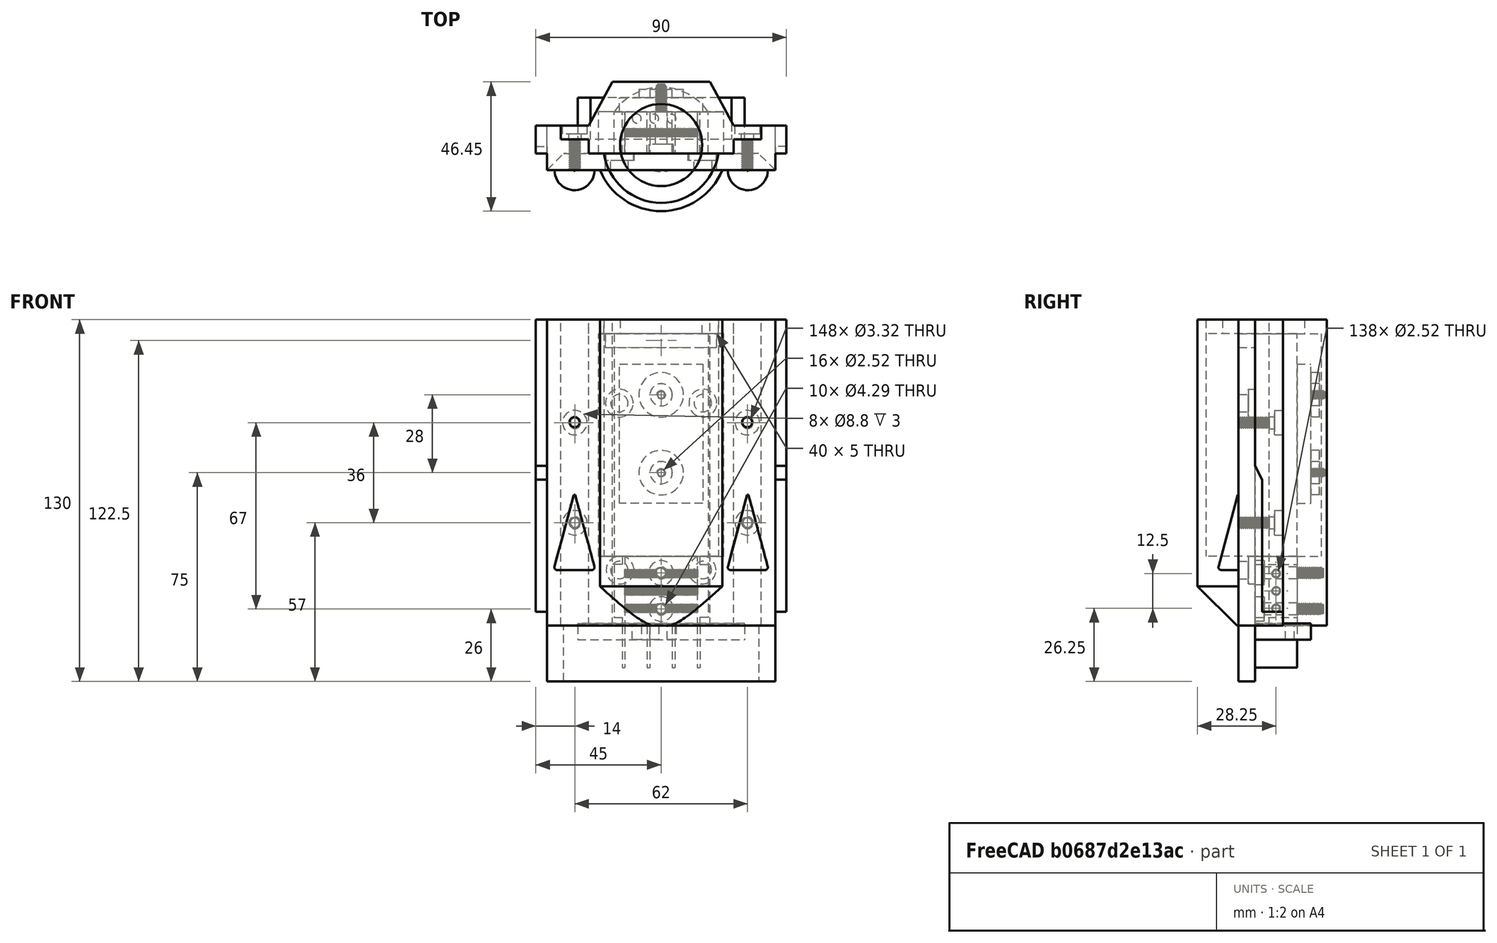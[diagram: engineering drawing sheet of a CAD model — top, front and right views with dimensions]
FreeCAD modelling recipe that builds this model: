
FCSTD DOCUMENT  (FreeCAD 2023.131R26244 +5365 (Git))
Label: Ego 56v Battery mount
License: All rights reserved
LicenseURL: http://en.wikipedia.org/wiki/All_rights_reserved
objects: Sketcher::SketchObject×39, PartDesign::Pocket×22, PartDesign::Pad×11, PartDesign::Body×7, PartDesign::Hole×6, PartDesign::Chamfer×2, Spreadsheet::Sheet×1, PartDesign::Fillet×1
note: 211 computed .brp shape members not serialized (recipe doc carries the construction recipe); baked Part::Feature solids carry a one-line shape summary decoded from their .brp

FEATURE [Sketcher::SketchObject] Sketch
  ArcFitTolerance = 1e-06
  AttachmentSupport = -> [XY_Plane]
  ExternalBSplineMaxDegree = 5
  ExternalBSplineTolerance = 0.0001
  FullyConstrained = false
  InternalTolerance = 1e-06
  InvalidShape = false
  MakeInternals = false
  MapMode = 5
  Support = -> [XY_Plane]
  TreeRank = 13
  ValidateShape = true
  sketch-geometry (12):
    g0: LineSegment StartX=-17.5 StartY=25.7 StartZ=0 EndX=17.5 EndY=25.7 EndZ=0
    g1: LineSegment StartX=-17.5 StartY=25.7 StartZ=0 EndX=-26 EndY=10 EndZ=0
    g2: LineSegment StartX=17.5 StartY=25.7 StartZ=0 EndX=26 EndY=10 EndZ=0
    g3: LineSegment StartX=-26 StartY=10 StartZ=0 EndX=-45 EndY=10 EndZ=0
    g4: LineSegment StartX=26 StartY=10 StartZ=0 EndX=45 EndY=10 EndZ=0
    g5: LineSegment StartX=-41 StartY=-6 StartZ=0 EndX=41 EndY=-6 EndZ=0
    g6: LineSegment StartX=-45 StartY=10 StartZ=0 EndX=-45 EndY=0 EndZ=0
    g7: LineSegment StartX=-45 StartY=-9e-16 StartZ=0 EndX=-41 EndY=-9e-16 EndZ=0
    g8: LineSegment StartX=-41 StartY=-6 StartZ=0 EndX=-41 EndY=-9e-16 EndZ=0
    g9: LineSegment StartX=45 StartY=10 StartZ=0 EndX=45 EndY=0 EndZ=0
    g10: LineSegment StartX=45 StartY=0 StartZ=0 EndX=41 EndY=0 EndZ=0
    g11: LineSegment StartX=41 StartY=-6 StartZ=0 EndX=41 EndY=0 EndZ=0
  constraints (33):
    c: DistanceX(g0,g0) = 35
    c: Symmetric(g0,g0,g-2)
    c: Coincident(g1,g0)
    c: Coincident(g2,g0)
    c: DistanceY(g2,g0) = 15.7
    c: Symmetric(g1,g2,g-2)
    c: DistanceX(g1,g2) = 52
    c: Coincident(g3,g1)
    c: Horizontal(g3)
    c: Coincident(g4,g2)
    c: Horizontal(g4)
    c: Equal(g3,g4)
    c: DistanceY(g5,g4) = 16
    c: DistanceX(g3,g4) = 90
    c: DistanceX(g5,g5) = 82
    c: Coincident(g6,g3)
    c: Vertical(g6)
    c: Coincident(g7,g6)
    c: Horizontal(g7)
    c: Coincident(g8,g5)
    c: Coincident(g8,g7)
    c: Vertical(g8)
    c: Coincident(g9,g4)
    c: Vertical(g9)
    c: Coincident(g10,g9)
    c: Horizontal(g10)
    c: Coincident(g11,g5)
    c: Coincident(g11,g10)
    c: Vertical(g11)
    c: Equal(g6,g9)
    c: Equal(g8,g11)
    c: DistanceY(g9,g4) = 10
    c: PointOnObject(g10,g-1)
FEATURE [PartDesign::Pad] Pad
  AddSubType = 0
  AlongSketchNormal = false
  AutoTaperInnerAngle = true
  CheckUpToFaceLimits = true
  ClaimChildren = false
  Direction = (0,0,1)
  Fit = 0
  FitJoin = 0
  InnerFit = 0
  InnerFitJoin = 0
  InvalidShape = false
  Length = 110
  Length2 = 100
  Linearize = true
  NewSolid = false
  Profile = -> Sketch
  Suppress = false
  TaperInnerAngle = 0
  TaperInnerAngleRev = 0
  TreeRank = 14
  Type = 0
  ValidateShape = true
  _ProfileBasedVersion = 1
FEATURE [Sketcher::SketchObject] Sketch001
  ArcFitTolerance = 1e-06
  AttachmentOffset = pos=(0,0,-45) rot=(0,0,1;0rad)
  AttachmentSupport = -> [YZ_Plane]
  ExternalBSplineMaxDegree = 5
  ExternalBSplineTolerance = 0.0001
  FullyConstrained = true
  InternalTolerance = 1e-06
  InvalidShape = false
  MakeInternals = false
  MapMode = 5
  Placement = pos=(-45,1e-14,-1e-14) rot=(0.57735,0.57735,0.57735;2.0944rad)
  Support = -> [YZ_Plane]
  TreeRank = 15
  ValidateShape = true
  sketch-geometry (6):
    g0: LineSegment StartX=2.5 StartY=5 StartZ=0 EndX=10 EndY=5 EndZ=0
    g1: LineSegment StartX=0 StartY=0 StartZ=0 EndX=10 EndY=0 EndZ=0
    g2: LineSegment StartX=10 StartY=5 StartZ=0 EndX=10 EndY=0 EndZ=0
    g3: LineSegment StartX=2.5 StartY=5 StartZ=0 EndX=2.5 EndY=52.5 EndZ=0
    g4: LineSegment StartX=2.5 StartY=52.5 StartZ=0 EndX=0 EndY=57.5 EndZ=0
    g5: LineSegment StartX=0 StartY=57.5 StartZ=0 EndX=0 EndY=0 EndZ=0
  constraints (17):
    c: Horizontal(g0)
    c: DistanceY(g-1,g0) = 5
    c: Coincident(g1,g-1)
    c: PointOnObject(g1,g-1)
    c: Coincident(g2,g0)
    c: Coincident(g2,g1)
    c: Vertical(g2)
    c: DistanceX(g1,g1) = 10
    c: Coincident(g3,g0)
    c: Vertical(g3)
    c: DistanceY(g1,g3) = 52.5
    c: Coincident(g4,g3)
    c: PointOnObject(g4,g-2)
    c: DistanceY(g3,g4) = 5
    c: Coincident(g5,g4)
    c: Coincident(g5,g1)
    c: DistanceX(g1,g0) = 2.5
FEATURE [PartDesign::Pocket] Pocket
  AddSubType = 1
  AutoTaperInnerAngle = true
  BaseFeature = -> Pad
  CheckUpToFaceLimits = true
  ClaimChildren = false
  Fit = 0
  FitJoin = 0
  InnerFit = 0
  InnerFitJoin = 0
  InvalidShape = false
  Length = 4
  Length2 = 100
  Linearize = true
  NewSolid = false
  Profile = -> Sketch001
  Reversed = true
  Suppress = false
  TaperInnerAngle = 0
  TaperInnerAngleRev = 0
  TreeRank = 16
  Type = 0
  ValidateShape = true
  _ProfileBasedVersion = 1
  _Version = 1
FEATURE [Sketcher::SketchObject] Sketch002
  ArcFitTolerance = 1e-06
  AttachmentOffset = pos=(0,0,45) rot=(0,0,1;0rad)
  AttachmentSupport = -> [YZ_Plane]
  ExternalBSplineMaxDegree = 5
  ExternalBSplineTolerance = 0.0001
  FullyConstrained = true
  InternalTolerance = 1e-06
  InvalidShape = false
  MakeInternals = false
  MapMode = 5
  Placement = pos=(45,-1e-14,1e-14) rot=(0.57735,0.57735,0.57735;2.0944rad)
  Support = -> [YZ_Plane]
  TreeRank = 17
  ValidateShape = true
  sketch-geometry (6):
    g0: LineSegment StartX=2.5 StartY=5 StartZ=0 EndX=10 EndY=5 EndZ=0
    g1: LineSegment StartX=0 StartY=0 StartZ=0 EndX=10 EndY=0 EndZ=0
    g2: LineSegment StartX=10 StartY=5 StartZ=0 EndX=10 EndY=0 EndZ=0
    g3: LineSegment StartX=2.5 StartY=5 StartZ=0 EndX=2.5 EndY=52.5 EndZ=0
    g4: LineSegment StartX=2.5 StartY=52.5 StartZ=0 EndX=0 EndY=57.5 EndZ=0
    g5: LineSegment StartX=0 StartY=57.5 StartZ=0 EndX=0 EndY=0 EndZ=0
  constraints (17):
    c: Horizontal(g0)
    c: DistanceY(g-1,g0) = 5
    c: Coincident(g1,g-1)
    c: PointOnObject(g1,g-1)
    c: Coincident(g2,g0)
    c: Coincident(g2,g1)
    c: Vertical(g2)
    c: DistanceX(g1,g1) = 10
    c: Coincident(g3,g0)
    c: Vertical(g3)
    c: DistanceY(g1,g3) = 52.5
    c: Coincident(g4,g3)
    c: PointOnObject(g4,g-2)
    c: DistanceY(g3,g4) = 5
    c: Coincident(g5,g4)
    c: Coincident(g5,g1)
    c: DistanceX(g1,g0) = 2.5
FEATURE [PartDesign::Pocket] Pocket002
  AddSubType = 1
  AutoTaperInnerAngle = true
  BaseFeature = -> Pocket
  CheckUpToFaceLimits = true
  ClaimChildren = false
  Fit = 0
  FitJoin = 0
  InnerFit = 0
  InnerFitJoin = 0
  InvalidShape = false
  Length = 4
  Length2 = 100
  Linearize = true
  NewSolid = false
  Profile = -> Sketch002
  Suppress = false
  TaperInnerAngle = 0
  TaperInnerAngleRev = 0
  TreeRank = 20
  Type = 0
  ValidateShape = true
  _ProfileBasedVersion = 1
  _Version = 1
FEATURE [Sketcher::SketchObject] Sketch003
  ArcFitTolerance = 1e-06
  AttachmentSupport = -> [XY_Plane]
  ExternalBSplineMaxDegree = 5
  ExternalBSplineTolerance = 0.0001
  FullyConstrained = true
  InternalTolerance = 1e-06
  InvalidShape = false
  MakeInternals = false
  MapMode = 5
  Support = -> [XY_Plane]
  TreeRank = 21
  ValidateShape = true
  sketch-geometry (16):
    g0: LineSegment StartX=-13 StartY=0 StartZ=0 EndX=-14 EndY=0 EndZ=0
    g1: LineSegment StartX=-14 StartY=0 StartZ=0 EndX=-14 EndY=15 EndZ=0
    g2: LineSegment StartX=-14 StartY=15 StartZ=0 EndX=-13 EndY=15 EndZ=0
    g3: LineSegment StartX=-13 StartY=15 StartZ=0 EndX=-13 EndY=0 EndZ=0
    g4: LineSegment StartX=-4 StartY=0 StartZ=0 EndX=-5 EndY=0 EndZ=0
    g5: LineSegment StartX=-5 StartY=0 StartZ=0 EndX=-5 EndY=15 EndZ=0
    g6: LineSegment StartX=-5 StartY=15 StartZ=0 EndX=-4 EndY=15 EndZ=0
    g7: LineSegment StartX=-4 StartY=15 StartZ=0 EndX=-4 EndY=0 EndZ=0
    g8: LineSegment StartX=5 StartY=0 StartZ=0 EndX=4 EndY=0 EndZ=0
    g9: LineSegment StartX=4 StartY=0 StartZ=0 EndX=4 EndY=15 EndZ=0
    g10: LineSegment StartX=4 StartY=15 StartZ=0 EndX=5 EndY=15 EndZ=0
    g11: LineSegment StartX=5 StartY=15 StartZ=0 EndX=5 EndY=0 EndZ=0
    g12: LineSegment StartX=13 StartY=0 StartZ=0 EndX=14 EndY=0 EndZ=0
    g13: LineSegment StartX=14 StartY=0 StartZ=0 EndX=14 EndY=15 EndZ=0
    g14: LineSegment StartX=14 StartY=15 StartZ=0 EndX=13 EndY=15 EndZ=0
    g15: LineSegment StartX=13 StartY=15 StartZ=0 EndX=13 EndY=0 EndZ=0
  constraints (47):
    c: Coincident(g0,g1)
    c: Coincident(g1,g2)
    c: Coincident(g2,g3)
    c: Coincident(g3,g0)
    c: Horizontal(g0)
    c: Horizontal(g2)
    c: Vertical(g1)
    c: Vertical(g3)
    c: Coincident(g4,g5)
    c: Coincident(g5,g6)
    c: Coincident(g6,g7)
    c: Coincident(g7,g4)
    c: Horizontal(g4)
    c: Horizontal(g6)
    c: Vertical(g5)
    c: Vertical(g7)
    c: Coincident(g8,g9)
    c: Coincident(g9,g10)
    c: Coincident(g10,g11)
    c: Coincident(g11,g8)
    c: Horizontal(g8)
    c: Horizontal(g10)
    c: Vertical(g9)
    c: Vertical(g11)
    c: Coincident(g12,g13)
    c: Coincident(g13,g14)
    c: Coincident(g14,g15)
    c: Coincident(g15,g12)
    c: Horizontal(g12)
    c: Horizontal(g14)
    c: Vertical(g13)
    c: Vertical(g15)
    c: Equal(g2,g6)
    c: Equal(g2,g10)
    c: Equal(g2,g14)
    c: DistanceX(g1,g5) = 9
    c: DistanceX(g5,g9) = 9
    c: DistanceX(g9,g14) = 9
    c: Symmetric(g6,g9,g-2)
    c: DistanceY(g4,g0) = 0
    c: DistanceY(g8,g4) = 0
    c: DistanceY(g12,g8) = 0
    c: DistanceY(g5,g2) = 0
    c: DistanceY(g10,g14) = 0
    c: DistanceX(g1,g2) = 1
    c: DistanceY(g0,g1) = 15
    c: PointOnObject(g0,g-1)
FEATURE [PartDesign::Pad] Pad001
  AddSubType = 0
  AlongSketchNormal = false
  AutoTaperInnerAngle = true
  BaseFeature = -> Pocket002
  CheckUpToFaceLimits = true
  ClaimChildren = false
  Direction = (0,0,1)
  Fit = 0
  FitJoin = 0
  InnerFit = 0
  InnerFitJoin = 0
  InvalidShape = false
  Length = 15
  Length2 = 100
  Linearize = true
  NewSolid = false
  Profile = -> Sketch003
  Reversed = true
  Suppress = false
  TaperInnerAngle = 0
  TaperInnerAngleRev = 0
  TreeRank = 22
  Type = 0
  ValidateShape = true
  _ProfileBasedVersion = 1
FEATURE [PartDesign::Body] Body  label="Template"
  AutoGroupSolids = false
  ClaimAllChildren = false
  ExportMode = 0
  Group = -> [Sketch,Pad,Sketch001,Pocket,Sketch002,Pocket002,Sketch003,Pad001]
  InvalidShape = false
  Origin = -> Origin
  Tip = -> Pad001
  TreeRank = 12
  ValidateShape = true
  _ExportChildren = -> [Pad,Pocket,Pocket002,Pad001]
  _GroupVersion = 1
FEATURE [Spreadsheet::Sheet] Spreadsheet  label="Parameters"
  PythonMode = false
  ShowCells = 0
  TreeRank = 11
  cells = A1=Thickness; B1(thickness)=3; A3=Screw Head Diameter; B3(screw_head_diameter)=8.5; A4=Screw Head Height; B4(screw_head_height)=3; A5=Screw Through Hole Diameter; B5(screw_hole_diameter)=4; A6=Screw Shaft Length; B6(screw_shaft_length)=8.5; A8=Copper Thickness; B8(copper_thickness)=0.8; A10=M2 Shaft Diameter; B10=1.86; C10(m2_shaft_diameter)==B10 * 1.1; A11=M2 Head Diameter; B11=3.2; C11(m2_head_diameter)==B11 * 1.1; A12=M2 Head Height; B12=1.25; C12(m2_head_height)==B12 * 1.1; A13=M2 Threaded Insert Diameter; C13(m2_insert_diameter)=2.81; A14=M2.5 Shaft Diameter; B14=2.43; C14(m2_5_shaft_diameter)==B14 * 1.1; A15=M2.5 Head Diameter; B15=4.15; C15(m2_5_head_diameter)==B15 * 1.1; A16=M2.5 Head Height; B16=1.65; C16(m2_5_head_height)==B16 * 1.1; A17=M2.5 Threaded Insert Diameter; C17(m2_5_insert_diameter)=3.04; A18=M3 Shaft Diameter; B18=2.9; C18(m3_shaft_diameter)==B18 * 1.1; A19=M3 Head Diameter; B19=5.35; C19(m3_head_diameter)==B19 * 1.1; A20=M3 Head Height; B20=2; C20(m3_head_height)==B20 * 1.1; A21=M3 Threaded Insert Diameter; C21(m3_insert_diameter)=3.74; A22=M4 Shaft Diameter; B22=3.9; C22(m4_shaft_diameter)==B22 * 1.1; A23=M4 Head Diameter; B23=8; C23(m4_head_diameter)==B23 * 1.1; A24=M4 Head Height; B24=2.85; C24(m4_head_height)==B24 * 1.1; A25=M4 Threaded Insert Diameter; C25(m4_insert_diameter)=5.33; A27=Charger Outer Diameter; B27(charger_outer_diameter)=36.75; C27=36.75; A28=Charger Hole Diameter; B28(charger_hole_diameter)=29.5; C28=28.55; A29=Charger Total Length; B29(charger_length)=50; C29=50; A30=Charger Hole Offset; B30(charger_offset)=-3
FEATURE [Sketcher::SketchObject] Sketch004
  ArcFitTolerance = 1e-06
  AttachmentSupport = -> [XY_Plane001]
  ExternalBSplineMaxDegree = 5
  ExternalBSplineTolerance = 0.0001
  FullyConstrained = true
  InternalTolerance = 1e-06
  InvalidShape = false
  MakeInternals = false
  MapMode = 5
  Support = -> [XY_Plane001]
  TreeRank = 34
  ValidateShape = true
  sketch-geometry (16):
    g0: LineSegment StartX=-36 StartY=10 StartZ=0 EndX=-45 EndY=10 EndZ=0
    g1: LineSegment StartX=36 StartY=10 StartZ=0 EndX=45 EndY=10 EndZ=0
    g2: LineSegment StartX=-41 StartY=-6 StartZ=0 EndX=41 EndY=-6 EndZ=0
    g3: LineSegment StartX=-45 StartY=10 StartZ=0 EndX=-45 EndY=0 EndZ=0
    g4: LineSegment StartX=-45 StartY=0 StartZ=0 EndX=-41 EndY=0 EndZ=0
    g5: LineSegment StartX=-41 StartY=-6 StartZ=0 EndX=-41 EndY=0 EndZ=0
    g6: LineSegment StartX=45 StartY=10 StartZ=0 EndX=45 EndY=0 EndZ=0
    g7: LineSegment StartX=45 StartY=0 StartZ=0 EndX=41 EndY=0 EndZ=0
    g8: LineSegment StartX=41 StartY=-6 StartZ=0 EndX=41 EndY=0 EndZ=0
    g9: LineSegment StartX=-26 StartY=0 StartZ=0 EndX=26 EndY=0 EndZ=0
    g10: LineSegment StartX=-26 StartY=0 StartZ=0 EndX=-26 EndY=5 EndZ=0
    g11: LineSegment StartX=26 StartY=0 StartZ=0 EndX=26 EndY=5 EndZ=0
    g12: LineSegment StartX=-26 StartY=5 StartZ=0 EndX=-36 EndY=5 EndZ=0
    g13: LineSegment StartX=-36 StartY=5 StartZ=0 EndX=-36 EndY=10 EndZ=0
    g14: LineSegment StartX=26 StartY=5 StartZ=0 EndX=36 EndY=5 EndZ=0
    g15: LineSegment StartX=36 StartY=5 StartZ=0 EndX=36 EndY=10 EndZ=0
  constraints (45):
    c: Symmetric(g0,g1,g-2)
    c: DistanceX(g0,g1) = 72
    c: Horizontal(g0)
    c: Horizontal(g1)
    c: Equal(g0,g1)
    c: DistanceY(g2,g1) = 16
    c: DistanceX(g0,g1) = 90
    c: DistanceX(g2,g2) = 82
    c: Coincident(g3,g0)
    c: Vertical(g3)
    c: Coincident(g4,g3)
    c: Horizontal(g4)
    c: Coincident(g5,g2)
    c: Coincident(g5,g4)
    c: Vertical(g5)
    c: Coincident(g6,g1)
    c: Vertical(g6)
    c: Coincident(g7,g6)
    c: Horizontal(g7)
    c: Coincident(g8,g2)
    c: Coincident(g8,g7)
    c: Vertical(g8)
    c: Equal(g3,g6)
    c: DistanceY(g6,g1) = 10
    c: PointOnObject(g7,g-1)
    c: PointOnObject(g9,g-1)
    c: Coincident(g10,g9)
    c: Vertical(g10)
    c: DistanceY(g9,g10) = 5
    c: Coincident(g11,g9)
    c: Vertical(g11)
    c: Equal(g10,g11)
    c: Symmetric(g9,g9,g-1)
    c: Coincident(g12,g10)
    c: Horizontal(g12)
    c: Coincident(g13,g12)
    c: Coincident(g13,g0)
    c: Vertical(g13)
    c: Coincident(g14,g11)
    c: Horizontal(g14)
    c: Coincident(g15,g14)
    c: Coincident(g15,g1)
    c: Vertical(g15)
    c: DistanceX(g9,g9) = 52
    c: Symmetric(g2,g2,g-2)
FEATURE [PartDesign::Pad] Pad002
  AddSubType = 0
  AlongSketchNormal = false
  AutoTaperInnerAngle = true
  CheckUpToFaceLimits = true
  ClaimChildren = false
  Direction = (0,0,1)
  Fit = 0
  FitJoin = 0
  InnerFit = 0
  InnerFitJoin = 0
  InvalidShape = false
  Length = 110
  Length2 = 100
  Linearize = true
  NewSolid = false
  Profile = -> Sketch004
  Suppress = false
  TaperInnerAngle = 0
  TaperInnerAngleRev = 0
  TreeRank = 35
  Type = 0
  ValidateShape = true
  _ProfileBasedVersion = 1
FEATURE [Sketcher::SketchObject] Sketch005
  ArcFitTolerance = 1e-06
  AttachmentOffset = pos=(0,0,-45) rot=(0,0,1;0rad)
  AttachmentSupport = -> [YZ_Plane001]
  ExternalBSplineMaxDegree = 5
  ExternalBSplineTolerance = 0.0001
  FullyConstrained = true
  InternalTolerance = 1e-06
  InvalidShape = false
  MakeInternals = false
  MapMode = 5
  Placement = pos=(-45,1e-14,-1e-14) rot=(0.57735,0.57735,0.57735;2.0944rad)
  Support = -> [YZ_Plane001]
  TreeRank = 15
  ValidateShape = true
  sketch-geometry (6):
    g0: LineSegment StartX=2.5 StartY=5 StartZ=0 EndX=10 EndY=5 EndZ=0
    g1: LineSegment StartX=0 StartY=0 StartZ=0 EndX=10 EndY=0 EndZ=0
    g2: LineSegment StartX=10 StartY=5 StartZ=0 EndX=10 EndY=0 EndZ=0
    g3: LineSegment StartX=2.5 StartY=5 StartZ=0 EndX=2.5 EndY=52.5 EndZ=0
    g4: LineSegment StartX=2.5 StartY=52.5 StartZ=0 EndX=0 EndY=57.5 EndZ=0
    g5: LineSegment StartX=0 StartY=57.5 StartZ=0 EndX=0 EndY=0 EndZ=0
  constraints (17):
    c: Horizontal(g0)
    c: DistanceY(g-1,g0) = 5
    c: Coincident(g1,g-1)
    c: PointOnObject(g1,g-1)
    c: Coincident(g2,g0)
    c: Coincident(g2,g1)
    c: Vertical(g2)
    c: DistanceX(g1,g1) = 10
    c: Coincident(g3,g0)
    c: Vertical(g3)
    c: DistanceY(g1,g3) = 52.5
    c: Coincident(g4,g3)
    c: PointOnObject(g4,g-2)
    c: DistanceY(g3,g4) = 5
    c: Coincident(g5,g4)
    c: Coincident(g5,g1)
    c: DistanceX(g1,g0) = 2.5
FEATURE [PartDesign::Pocket] Pocket003
  AddSubType = 1
  AutoTaperInnerAngle = true
  BaseFeature = -> Pad002
  CheckUpToFaceLimits = true
  ClaimChildren = false
  Fit = 0
  FitJoin = 0
  InnerFit = 0
  InnerFitJoin = 0
  InvalidShape = false
  Length = 4
  Length2 = 100
  Linearize = true
  NewSolid = false
  Profile = -> Sketch005
  Reversed = true
  Suppress = false
  TaperInnerAngle = 0
  TaperInnerAngleRev = 0
  TreeRank = 36
  Type = 0
  ValidateShape = true
  _ProfileBasedVersion = 1
  _Version = 1
FEATURE [Sketcher::SketchObject] Sketch006
  ArcFitTolerance = 1e-06
  AttachmentOffset = pos=(0,0,45) rot=(0,0,1;0rad)
  AttachmentSupport = -> [YZ_Plane001]
  ExternalBSplineMaxDegree = 5
  ExternalBSplineTolerance = 0.0001
  FullyConstrained = true
  InternalTolerance = 1e-06
  InvalidShape = false
  MakeInternals = false
  MapMode = 5
  Placement = pos=(45,-1e-14,1e-14) rot=(0.57735,0.57735,0.57735;2.0944rad)
  Support = -> [YZ_Plane001]
  TreeRank = 17
  ValidateShape = true
  sketch-geometry (6):
    g0: LineSegment StartX=2.5 StartY=5 StartZ=0 EndX=10 EndY=5 EndZ=0
    g1: LineSegment StartX=0 StartY=0 StartZ=0 EndX=10 EndY=0 EndZ=0
    g2: LineSegment StartX=10 StartY=5 StartZ=0 EndX=10 EndY=0 EndZ=0
    g3: LineSegment StartX=2.5 StartY=5 StartZ=0 EndX=2.5 EndY=52.5 EndZ=0
    g4: LineSegment StartX=2.5 StartY=52.5 StartZ=0 EndX=0 EndY=57.5 EndZ=0
    g5: LineSegment StartX=0 StartY=57.5 StartZ=0 EndX=0 EndY=0 EndZ=0
  constraints (17):
    c: Horizontal(g0)
    c: DistanceY(g-1,g0) = 5
    c: Coincident(g1,g-1)
    c: PointOnObject(g1,g-1)
    c: Coincident(g2,g0)
    c: Coincident(g2,g1)
    c: Vertical(g2)
    c: DistanceX(g1,g1) = 10
    c: Coincident(g3,g0)
    c: Vertical(g3)
    c: DistanceY(g1,g3) = 52.5
    c: Coincident(g4,g3)
    c: PointOnObject(g4,g-2)
    c: DistanceY(g3,g4) = 5
    c: Coincident(g5,g4)
    c: Coincident(g5,g1)
    c: DistanceX(g1,g0) = 2.5
FEATURE [PartDesign::Pocket] Pocket004
  AddSubType = 1
  AutoTaperInnerAngle = true
  BaseFeature = -> Pocket003
  CheckUpToFaceLimits = true
  ClaimChildren = false
  Fit = 0
  FitJoin = 0
  InnerFit = 0
  InnerFitJoin = 0
  InvalidShape = false
  Length = 4
  Length2 = 100
  Linearize = true
  NewSolid = false
  Profile = -> Sketch006
  Suppress = false
  TaperInnerAngle = 0
  TaperInnerAngleRev = 0
  TreeRank = 37
  Type = 0
  ValidateShape = true
  _ProfileBasedVersion = 1
  _Version = 1
FEATURE [Sketcher::SketchObject] Sketch007
  ArcFitTolerance = 1e-06
  AttachmentOffset = pos=(0,0,-10) rot=(0,0,1;0rad)
  AttachmentSupport = -> [XZ_Plane001]
  ExternalBSplineMaxDegree = 5
  ExternalBSplineTolerance = 0.0001
  FullyConstrained = false
  InternalTolerance = 1e-06
  InvalidShape = false
  MakeInternals = false
  MapMode = 5
  Placement = pos=(0,10,-2.2e-15) rot=(1,0,0;1.5708rad)
  Support = -> [XZ_Plane001]
  TreeRank = 38
  ValidateShape = true
  expr: Constraints[6] = 110 - 37
  sketch-geometry (4):
    g0: Circle CenterX=31 CenterY=73 CenterZ=0 NormalX=0 NormalY=0 NormalZ=1 AngleXU=0 Radius=2.68754
    g1: Circle CenterX=31 CenterY=37 CenterZ=0 NormalX=0 NormalY=0 NormalZ=1 AngleXU=0 Radius=2.68754
    g2: Circle CenterX=-31 CenterY=37 CenterZ=0 NormalX=0 NormalY=0 NormalZ=1 AngleXU=0 Radius=2.68754
    g3: Circle CenterX=-31 CenterY=73 CenterZ=0 NormalX=0 NormalY=0 NormalZ=1 AngleXU=0 Radius=2.68754
  constraints (9):
    c: Equal(g0,g3)
    c: Equal(g0,g1)
    c: Equal(g0,g2)
    c: Symmetric(g0,g3,g-2)
    c: Symmetric(g1,g2,g-2)
    c: DistanceY(g-1,g1) = 37
    c: DistanceY(g-1,g0) = 73
    c: DistanceX(g3,g0) = 62
    c: DistanceX(g2,g3) = 0
FEATURE [PartDesign::Hole] Hole
  AddSubType = 1
  BaseFeature = -> Pocket004
  ClaimChildren = false
  CustomThreadClearance = 0
  Depth = 25
  DepthType = 0
  Diameter = 3.322
  DrillForDepth = false
  DrillPoint = 1
  DrillPointAngle = 118
  Fit = 0
  FitJoin = 0
  HoleCutCountersinkAngle = 90
  HoleCutCustomValues = false
  HoleCutDepth = 0
  HoleCutDiameter = 6.1
  HoleCutType = 0
  InnerFit = 0
  InnerFitJoin = 0
  InvalidShape = false
  Linearize = true
  ModelThread = true
  NewSolid = false
  Profile = -> Sketch007
  Reversed = true
  Suppress = false
  Tapered = false
  TaperedAngle = 90
  ThreadClass = 0
  ThreadDepth = 25
  ThreadDepthType = 0
  ThreadDirection = 0
  ThreadFit = 0
  ThreadSize = 11
  ThreadType = 1
  Threaded = true
  TreeRank = 39
  UseCustomThreadClearance = false
  ValidateShape = true
  _ProfileBasedVersion = 1
FEATURE [Sketcher::SketchObject] Sketch012
  ArcFitTolerance = 1e-06
  AttachmentSupport = -> [XZ_Plane001]
  ExternalBSplineMaxDegree = 5
  ExternalBSplineTolerance = 0.0001
  FullyConstrained = true
  InternalTolerance = 1e-06
  InvalidShape = false
  MakeInternals = false
  MapMode = 5
  Placement = pos=(0,0,0) rot=(1,0,0;1.5708rad)
  Support = -> [XZ_Plane001]
  TreeRank = 58
  ValidateShape = true
  sketch-geometry (4):
    g0: LineSegment StartX=-20 StartY=105 StartZ=0 EndX=20 EndY=105 EndZ=0
    g1: LineSegment StartX=20 StartY=105 StartZ=0 EndX=20 EndY=100 EndZ=0
    g2: LineSegment StartX=20 StartY=100 StartZ=0 EndX=-20 EndY=100 EndZ=0
    g3: LineSegment StartX=-20 StartY=100 StartZ=0 EndX=-20 EndY=105 EndZ=0
  constraints (11):
    c: Coincident(g0,g1)
    c: Coincident(g1,g2)
    c: Coincident(g2,g3)
    c: Coincident(g3,g0)
    c: Horizontal(g2)
    c: Vertical(g1)
    c: Vertical(g3)
    c: Symmetric(g0,g0,g-2)
    c: DistanceY(g-1,g0) = 105
    c: DistanceY(g1,g0) = 5
    c: DistanceX(g0,g0) = 40
FEATURE [PartDesign::Pocket] Pocket008
  AddSubType = 1
  AutoTaperInnerAngle = true
  BaseFeature = -> Hole
  CheckUpToFaceLimits = true
  ClaimChildren = false
  Fit = 0
  FitJoin = 0
  InnerFit = 0
  InnerFitJoin = 0
  InvalidShape = false
  Length = 100
  Length2 = 100
  Linearize = true
  NewSolid = false
  Profile = -> Sketch012
  Suppress = false
  TaperInnerAngle = 0
  TaperInnerAngleRev = 0
  TreeRank = 59
  Type = 4
  ValidateShape = true
  _ProfileBasedVersion = 1
  _Version = 1
FEATURE [Sketcher::SketchObject] Sketch014
  ArcFitTolerance = 1e-06
  AttachmentSupport = -> [XZ_Plane001]
  ExternalBSplineMaxDegree = 5
  ExternalBSplineTolerance = 0.0001
  FullyConstrained = true
  InternalTolerance = 1e-06
  InvalidShape = false
  MakeInternals = false
  MapMode = 5
  Placement = pos=(0,0,0) rot=(1,0,0;1.5708rad)
  Support = -> [XZ_Plane001]
  TreeRank = 62
  ValidateShape = true
  sketch-geometry (4):
    g0: Circle CenterX=15 CenterY=80 CenterZ=0 NormalX=0 NormalY=0 NormalZ=1 AngleXU=0 Radius=3.125
    g1: Circle CenterX=-15 CenterY=80 CenterZ=0 NormalX=0 NormalY=0 NormalZ=1 AngleXU=0 Radius=3.125
    g2: Circle CenterX=15 CenterY=20 CenterZ=0 NormalX=0 NormalY=0 NormalZ=1 AngleXU=0 Radius=3.125
    g3: Circle CenterX=-15 CenterY=20 CenterZ=0 NormalX=0 NormalY=0 NormalZ=1 AngleXU=0 Radius=3.125
  constraints (10):
    c: Equal(g0,g1)
    c: Equal(g0,g2)
    c: Equal(g0,g3)
    c: Symmetric(g0,g1,g-2)
    c: Symmetric(g2,g3,g-2)
    c: Diameter(g0) = 6.25
    c: DistanceX(g0,g2) = 0
    c: DistanceY(g-1,g3) = 20
    c: DistanceY(g-1,g0) = 80
    c: DistanceX(g1,g0) = 30
FEATURE [PartDesign::Pocket] Pocket010
  AddSubType = 1
  AutoTaperInnerAngle = true
  BaseFeature = -> Pocket008
  CheckUpToFaceLimits = true
  ClaimChildren = false
  Fit = 0
  FitJoin = 0
  InnerFit = 0
  InnerFitJoin = 0
  InvalidShape = false
  Length = 100
  Length2 = 100
  Linearize = true
  NewSolid = false
  Profile = -> Sketch014
  Reversed = true
  Suppress = false
  TaperInnerAngle = 0
  TaperInnerAngleRev = 0
  TreeRank = 63
  Type = 0
  ValidateShape = true
  _ProfileBasedVersion = 1
  _Version = 1
FEATURE [Sketcher::SketchObject] Sketch015
  ArcFitTolerance = 1e-06
  AttachmentSupport = -> [XZ_Plane001]
  ExternalBSplineMaxDegree = 5
  ExternalBSplineTolerance = 0.0001
  FullyConstrained = false
  InternalTolerance = 1e-06
  InvalidShape = false
  MakeInternals = false
  MapMode = 5
  Placement = pos=(0,0,0) rot=(1,0,0;1.5708rad)
  Support = -> [XZ_Plane001]
  TreeRank = 64
  ValidateShape = true
  sketch-geometry (4):
    g0: Circle CenterX=-15 CenterY=80 CenterZ=0 NormalX=0 NormalY=0 NormalZ=1 AngleXU=0 Radius=5
    g1: Circle CenterX=-14.7321 CenterY=20 CenterZ=0 NormalX=0 NormalY=0 NormalZ=1 AngleXU=0 Radius=5
    g2: Circle CenterX=14.7321 CenterY=20 CenterZ=0 NormalX=0 NormalY=0 NormalZ=1 AngleXU=0 Radius=5
    g3: Circle CenterX=15 CenterY=80 CenterZ=0 NormalX=0 NormalY=0 NormalZ=1 AngleXU=0 Radius=5
  constraints (9):
    c: Equal(g0,g3)
    c: Equal(g0,g1)
    c: Equal(g0,g2)
    c: Symmetric(g0,g3,g-2)
    c: Symmetric(g1,g2,g-2)
    c: Diameter(g0) = 10
    c: DistanceY(g-1,g1) = 20
    c: DistanceY(g-1,g0) = 80
    c: DistanceX(g0,g3) = 30
FEATURE [PartDesign::Pocket] Pocket011
  AddSubType = 1
  AutoTaperInnerAngle = true
  BaseFeature = -> Pocket010
  CheckUpToFaceLimits = true
  ClaimChildren = false
  Fit = 0
  FitJoin = 0
  InnerFit = 0
  InnerFitJoin = 0
  InvalidShape = false
  Length = 2.5
  Length2 = 100
  Linearize = true
  NewSolid = false
  Profile = -> Sketch015
  Reversed = true
  Suppress = false
  TaperInnerAngle = 0
  TaperInnerAngleRev = 0
  TreeRank = 65
  Type = 0
  ValidateShape = true
  _ProfileBasedVersion = 1
  _Version = 1
FEATURE [PartDesign::Body] Body001  label="Three Piece - A"
  AutoGroupSolids = false
  ClaimAllChildren = false
  ExportMode = 0
  Group = -> [Sketch004,Pad002,Pocket003,Pocket004,Sketch005,Sketch006,Sketch007,Hole,Sketch012,Pocket008,Sketch014,Pocket010,Sketch015,Pocket011]
  InvalidShape = false
  Origin = -> Origin001
  Tip = -> Pocket011
  TreeRank = 33
  ValidateShape = true
  _ExportChildren = -> [Pad002,Pocket003,Pocket004,Hole,Pocket008,Pocket010,Pocket011]
  _GroupVersion = 1
FEATURE [Sketcher::SketchObject] Sketch016
  ArcFitTolerance = 1e-06
  AttachmentSupport = -> [XY_Plane003]
  ExternalBSplineMaxDegree = 5
  ExternalBSplineTolerance = 0.0001
  FullyConstrained = true
  InternalTolerance = 1e-06
  InvalidShape = false
  MakeInternals = false
  MapMode = 5
  Support = -> [XY_Plane003]
  TreeRank = 50
  ValidateShape = true
  sketch-geometry (12):
    g0: LineSegment StartX=-17.5 StartY=25.7 StartZ=0 EndX=17.5 EndY=25.7 EndZ=0
    g1: LineSegment StartX=-17.5 StartY=25.7 StartZ=0 EndX=-26 EndY=10 EndZ=0
    g2: LineSegment StartX=17.5 StartY=25.7 StartZ=0 EndX=26 EndY=10 EndZ=0
    g3: LineSegment StartX=-26 StartY=10 StartZ=0 EndX=-36 EndY=10 EndZ=0
    g4: LineSegment StartX=26 StartY=10 StartZ=0 EndX=36 EndY=10 EndZ=0
    g5: LineSegment StartX=-36 StartY=10 StartZ=0 EndX=-36 EndY=5 EndZ=0
    g6: LineSegment StartX=-36 StartY=5 StartZ=0 EndX=-26 EndY=5 EndZ=0
    g7: LineSegment StartX=-26 StartY=5 StartZ=0 EndX=-26 EndY=0 EndZ=0
    g8: LineSegment StartX=36 StartY=10 StartZ=0 EndX=36 EndY=5 EndZ=0
    g9: LineSegment StartX=36 StartY=5 StartZ=0 EndX=26 EndY=5 EndZ=0
    g10: LineSegment StartX=26 StartY=5 StartZ=0 EndX=26 EndY=0 EndZ=0
    g11: LineSegment StartX=26 StartY=0 StartZ=0 EndX=-26 EndY=0 EndZ=0
  constraints (34):
    c: DistanceX(g0,g0) = 35
    c: Symmetric(g0,g0,g-2)
    c: Coincident(g1,g0)
    c: Coincident(g2,g0)
    c: DistanceY(g2,g0) = 15.7
    c: Symmetric(g1,g2,g-2)
    c: DistanceX(g1,g2) = 52
    c: Coincident(g3,g1)
    c: Horizontal(g3)
    c: Coincident(g4,g2)
    c: Horizontal(g4)
    c: Equal(g3,g4)
    c: DistanceX(g3,g4) = 72
    c: Coincident(g5,g3)
    c: Vertical(g5)
    c: Coincident(g6,g5)
    c: Horizontal(g6)
    c: Coincident(g7,g6)
    c: PointOnObject(g7,g-1)
    c: Vertical(g7)
    c: DistanceY(g5,g3) = 5
    c: DistanceX(g5,g6) = 10
    c: DistanceY(g7,g6) = 5
    c: Coincident(g8,g4)
    c: Vertical(g8)
    c: Coincident(g9,g8)
    c: Horizontal(g9)
    c: Coincident(g10,g9)
    c: PointOnObject(g10,g-1)
    c: Vertical(g10)
    c: Coincident(g11,g10)
    c: Coincident(g11,g7)
    c: Equal(g5,g8)
    c: Equal(g6,g9)
FEATURE [PartDesign::Pad] Pad004
  AddSubType = 0
  AlongSketchNormal = false
  AutoTaperInnerAngle = true
  CheckUpToFaceLimits = true
  ClaimChildren = false
  Direction = (0,0,1)
  Fit = 0
  FitJoin = 0
  InnerFit = 0
  InnerFitJoin = 0
  InvalidShape = false
  Length = 110
  Length2 = 100
  Linearize = true
  NewSolid = false
  Profile = -> Sketch016
  Suppress = false
  TaperInnerAngle = 0
  TaperInnerAngleRev = 0
  TreeRank = 76
  Type = 0
  ValidateShape = true
  _ProfileBasedVersion = 1
FEATURE [Sketcher::SketchObject] Sketch018
  ArcFitTolerance = 1e-06
  AttachmentOffset = pos=(0,0,-10) rot=(0,0,1;0rad)
  AttachmentSupport = -> [XZ_Plane003]
  ExternalBSplineMaxDegree = 5
  ExternalBSplineTolerance = 0.0001
  FullyConstrained = true
  InternalTolerance = 1e-06
  InvalidShape = false
  MakeInternals = false
  MapMode = 5
  Placement = pos=(0,10,-2.2e-15) rot=(1,0,0;1.5708rad)
  Support = -> [XZ_Plane003]
  TreeRank = 52
  ValidateShape = true
  expr: Constraints[6] = 110 - 37
  expr: Constraints[8] = <<Parameters>>.m4_head_diameter
  sketch-geometry (4):
    g0: Circle CenterX=31 CenterY=73 CenterZ=0 NormalX=0 NormalY=0 NormalZ=1 AngleXU=0 Radius=4.4
    g1: Circle CenterX=31 CenterY=37 CenterZ=0 NormalX=0 NormalY=0 NormalZ=1 AngleXU=0 Radius=4.4
    g2: Circle CenterX=-31 CenterY=37 CenterZ=0 NormalX=0 NormalY=0 NormalZ=1 AngleXU=0 Radius=4.4
    g3: Circle CenterX=-31 CenterY=73 CenterZ=0 NormalX=0 NormalY=0 NormalZ=1 AngleXU=0 Radius=4.4
  constraints (10):
    c: Equal(g0,g3)
    c: Equal(g0,g1)
    c: Equal(g0,g2)
    c: Symmetric(g0,g3,g-2)
    c: Symmetric(g1,g2,g-2)
    c: DistanceY(g-1,g1) = 37
    c: DistanceY(g-1,g0) = 73
    c: DistanceX(g3,g0) = 62
    c: Diameter(g3) = 8.8
    c: DistanceX(g2,g3) = 0
FEATURE [PartDesign::Pocket] Pocket012
  AddSubType = 1
  AutoTaperInnerAngle = true
  BaseFeature = -> Pad004
  CheckUpToFaceLimits = true
  ClaimChildren = false
  Fit = 0
  FitJoin = 0
  InnerFit = 0
  InnerFitJoin = 0
  InvalidShape = false
  Length = 3
  Length2 = 100
  Linearize = true
  NewSolid = false
  Profile = -> Sketch018
  Reversed = true
  Suppress = false
  TaperInnerAngle = 0
  TaperInnerAngleRev = 0
  TreeRank = 78
  Type = 0
  ValidateShape = true
  _ProfileBasedVersion = 1
  _Version = 1
  expr: Length = <<Parameters>>.screw_head_height
FEATURE [Sketcher::SketchObject] Sketch019
  ArcFitTolerance = 1e-06
  AttachmentOffset = pos=(0,0,-10) rot=(0,0,1;0rad)
  AttachmentSupport = -> [XZ_Plane003]
  ExternalBSplineMaxDegree = 5
  ExternalBSplineTolerance = 0.0001
  FullyConstrained = true
  InternalTolerance = 1e-06
  InvalidShape = false
  MakeInternals = false
  MapMode = 5
  Placement = pos=(0,10,-2.2e-15) rot=(1,0,0;1.5708rad)
  Support = -> [XZ_Plane003]
  TreeRank = 54
  ValidateShape = true
  expr: Constraints[6] = 110 - 37
  expr: Constraints[8] = <<Parameters>>.m4_shaft_diameter
  sketch-geometry (4):
    g0: Circle CenterX=31 CenterY=73 CenterZ=0 NormalX=0 NormalY=0 NormalZ=1 AngleXU=0 Radius=2.145
    g1: Circle CenterX=31 CenterY=37 CenterZ=0 NormalX=0 NormalY=0 NormalZ=1 AngleXU=0 Radius=2.145
    g2: Circle CenterX=-31 CenterY=37 CenterZ=0 NormalX=0 NormalY=0 NormalZ=1 AngleXU=0 Radius=2.145
    g3: Circle CenterX=-31 CenterY=73 CenterZ=0 NormalX=0 NormalY=0 NormalZ=1 AngleXU=0 Radius=2.145
  constraints (10):
    c: Equal(g0,g3)
    c: Equal(g0,g1)
    c: Equal(g0,g2)
    c: Symmetric(g0,g3,g-2)
    c: Symmetric(g1,g2,g-2)
    c: DistanceY(g-1,g1) = 37
    c: DistanceY(g-1,g0) = 73
    c: DistanceX(g3,g0) = 62
    c: Diameter(g3) = 4.29
    c: DistanceX(g2,g3) = 0
FEATURE [PartDesign::Pocket] Pocket013
  AddSubType = 1
  AutoTaperInnerAngle = true
  BaseFeature = -> Pocket012
  CheckUpToFaceLimits = true
  ClaimChildren = false
  Fit = 0
  FitJoin = 0
  InnerFit = 0
  InnerFitJoin = 0
  InvalidShape = false
  Length = 5
  Length2 = 100
  Linearize = true
  NewSolid = false
  Profile = -> Sketch019
  Reversed = true
  Suppress = false
  TaperInnerAngle = 0
  TaperInnerAngleRev = 0
  TreeRank = 79
  Type = 0
  ValidateShape = true
  _ProfileBasedVersion = 1
  _Version = 1
FEATURE [Sketcher::SketchObject] Sketch020
  ArcFitTolerance = 1e-06
  AttachmentSupport = -> [XZ_Plane003]
  ExternalBSplineMaxDegree = 5
  ExternalBSplineTolerance = 0.0001
  FullyConstrained = true
  InternalTolerance = 1e-06
  InvalidShape = false
  MakeInternals = false
  MapMode = 5
  Placement = pos=(0,0,0) rot=(1,0,0;1.5708rad)
  Support = -> [XZ_Plane003]
  TreeRank = 56
  ValidateShape = true
  sketch-geometry (18):
    g0: LineSegment StartX=-13.9 StartY=25 StartZ=0 EndX=-22.5 EndY=25 EndZ=0
    g1: LineSegment StartX=13.9 StartY=25 StartZ=0 EndX=22.5 EndY=25 EndZ=0
    g2: LineSegment StartX=-22.5 StartY=25 StartZ=0 EndX=-22.5 EndY=105 EndZ=0
    g3: LineSegment StartX=22.5 StartY=25 StartZ=0 EndX=22.5 EndY=105 EndZ=0
    g4: LineSegment StartX=22.5 StartY=105 StartZ=0 EndX=-22.5 EndY=105 EndZ=0
    g5: LineSegment StartX=-13.9 StartY=0 StartZ=0 EndX=13.9 EndY=-4.2e-15 EndZ=0
    g6: LineSegment StartX=-13.9 StartY=25 StartZ=0 EndX=-13.9 EndY=22 EndZ=0
    g7: LineSegment StartX=-13.9 StartY=22 StartZ=0 EndX=-16.9 EndY=22 EndZ=0
    g8: LineSegment StartX=-16.9 StartY=22 StartZ=0 EndX=-16.9 EndY=12.5 EndZ=0
    g9: LineSegment StartX=-16.9 StartY=12.5 StartZ=0 EndX=-16.9 EndY=3 EndZ=0
    g10: LineSegment StartX=-16.9 StartY=3 StartZ=0 EndX=-13.9 EndY=3 EndZ=0
    g11: LineSegment StartX=-13.9 StartY=3 StartZ=0 EndX=-13.9 EndY=0 EndZ=0
    g12: LineSegment StartX=13.9 StartY=25 StartZ=0 EndX=13.9 EndY=22 EndZ=0
    g13: LineSegment StartX=13.9 StartY=22 StartZ=0 EndX=16.9 EndY=22 EndZ=0
    g14: LineSegment StartX=16.9 StartY=22 StartZ=0 EndX=16.9 EndY=12.5 EndZ=0
    g15: LineSegment StartX=16.9 StartY=12.5 StartZ=0 EndX=16.9 EndY=3 EndZ=0
    g16: LineSegment StartX=16.9 StartY=3 StartZ=0 EndX=13.9 EndY=3 EndZ=0
    g17: LineSegment StartX=13.9 StartY=3 StartZ=0 EndX=13.9 EndY=-4.4e-15 EndZ=0
  constraints (53):
    c: Horizontal(g0)
    c: Horizontal(g1)
    c: Equal(g0,g1)
    c: Coincident(g2,g0)
    c: Vertical(g2)
    c: Coincident(g3,g1)
    c: Vertical(g3)
    c: Coincident(g4,g3)
    c: Coincident(g4,g2)
    c: Horizontal(g4)
    c: DistanceX(g2,g3) = 45
    c: DistanceY(g-1,g3) = 105
    c: PointOnObject(g5,g-1)
    c: DistanceX(g5,g5) = 27.8
    c: Symmetric(g5,g5,g-1)
    c: DistanceY(g5,g1) = 25
    c: Coincident(g6,g0)
    c: Vertical(g6)
    c: Coincident(g7,g6)
    c: Horizontal(g7)
    c: Coincident(g8,g7)
    c: Vertical(g8)
    c: Vertical(g9)
    c: Coincident(g10,g9)
    c: Horizontal(g10)
    c: Coincident(g11,g10)
    c: Coincident(g11,g5)
    c: Vertical(g11)
    c: Coincident(g12,g1)
    c: Vertical(g12)
    c: Coincident(g13,g12)
    c: Horizontal(g13)
    c: Coincident(g14,g13)
    c: Vertical(g14)
    c: Vertical(g15)
    c: Coincident(g16,g15)
    c: Horizontal(g16)
    c: Coincident(g17,g16)
    c: Coincident(g17,g5)
    c: Vertical(g17)
    c: Equal(g8,g9)
    c: Equal(g8,g14)
    c: Equal(g8,g15)
    c: Equal(g7,g10)
    c: Equal(g7,g13)
    c: Equal(g7,g16)
    c: DistanceY(g-1,g0) = 25
    c: Equal(g6,g11)
    c: Equal(g6,g12)
    c: DistanceX(g7,g6) = 3
    c: DistanceY(g5,g10) = 3
    c: Coincident(g9,g8)
    c: Coincident(g14,g15)
FEATURE [PartDesign::Pocket] Pocket014
  AddSubType = 1
  AutoTaperInnerAngle = true
  BaseFeature = -> Pocket013
  CheckUpToFaceLimits = true
  ClaimChildren = false
  Fit = 0
  FitJoin = 0
  InnerFit = 0
  InnerFitJoin = 0
  InvalidShape = false
  Length = 15
  Length2 = 100
  Linearize = true
  NewSolid = false
  Profile = -> Sketch020
  Suppress = false
  TaperInnerAngle = 0
  TaperInnerAngleRev = 0
  TreeRank = 80
  Type = 0
  ValidateShape = true
  _ProfileBasedVersion = 1
  _Version = 1
FEATURE [Sketcher::SketchObject] Sketch021
  ArcFitTolerance = 1e-06
  AttachmentOffset = pos=(0,0,-15) rot=(0,0,1;0rad)
  AttachmentSupport = -> [XZ_Plane003]
  ExternalBSplineMaxDegree = 5
  ExternalBSplineTolerance = 0.0001
  FullyConstrained = true
  InternalTolerance = 1e-06
  InvalidShape = false
  MakeInternals = false
  MapMode = 5
  Placement = pos=(0,15,-3.3e-15) rot=(1,0,0;1.5708rad)
  Support = -> [XZ_Plane003]
  TreeRank = 60
  ValidateShape = true
  expr: Constraints[3] = <<Parameters>>.m3_insert_diameter
  sketch-geometry (2):
    g0: Circle CenterX=0 CenterY=55 CenterZ=0 NormalX=0 NormalY=0 NormalZ=1 AngleXU=0 Radius=1.87
    g1: Circle CenterX=0 CenterY=83 CenterZ=0 NormalX=0 NormalY=0 NormalZ=1 AngleXU=0 Radius=1.87
  constraints (6):
    c: Equal(g1,g0)
    c: DistanceX(g1,g0) = 0
    c: DistanceX(g0,g-1) = 0
    c: Diameter(g1) = 3.74
    c: DistanceY(g0,g1) = 28
    c: DistanceY(g-1,g0) = 55
FEATURE [Sketcher::SketchObject] Sketch022
  ArcFitTolerance = 1e-06
  AttachmentSupport = -> [XZ_Plane003]
  ExternalBSplineMaxDegree = 5
  ExternalBSplineTolerance = 0.0001
  FullyConstrained = false
  InternalTolerance = 1e-06
  InvalidShape = false
  MakeInternals = false
  MapMode = 5
  Placement = pos=(0,0,0) rot=(1,0,0;1.5708rad)
  Support = -> [XZ_Plane003]
  TreeRank = 82
  ValidateShape = true
  sketch-geometry (2):
    g0: Circle CenterX=0 CenterY=19 CenterZ=0 NormalX=0 NormalY=0 NormalZ=1 AngleXU=0 Radius=1.85369
    g1: Circle CenterX=0 CenterY=6 CenterZ=0 NormalX=0 NormalY=0 NormalZ=1 AngleXU=0 Radius=1.85369
  constraints (5):
    c: PointOnObject(g0,g-2)
    c: PointOnObject(g1,g-2)
    c: Equal(g0,g1)
    c: DistanceY(g-1,g1) = 6
    c: DistanceY(g-1,g0) = 19
FEATURE [PartDesign::Hole] Hole001
  AddSubType = 1
  BaseFeature = -> Pocket014
  ClaimChildren = false
  CustomThreadClearance = 0
  Depth = 24.5
  DepthType = 0
  Diameter = 3.322
  DrillForDepth = false
  DrillPoint = 0
  DrillPointAngle = 118
  Fit = 0
  FitJoin = 0
  HoleCutCountersinkAngle = 90
  HoleCutCustomValues = false
  HoleCutDepth = 0
  HoleCutDiameter = 6.1
  HoleCutType = 0
  InnerFit = 0
  InnerFitJoin = 0
  InvalidShape = false
  Linearize = true
  ModelThread = true
  NewSolid = false
  Profile = -> Sketch022
  Suppress = false
  Tapered = false
  TaperedAngle = 90
  ThreadClass = 0
  ThreadDepth = 24.5
  ThreadDepthType = 0
  ThreadDirection = 0
  ThreadFit = 0
  ThreadSize = 11
  ThreadType = 1
  Threaded = true
  TreeRank = 83
  UseCustomThreadClearance = false
  ValidateShape = true
  _ProfileBasedVersion = 1
FEATURE [Sketcher::SketchObject] Sketch023
  ArcFitTolerance = 1e-06
  AttachmentSupport = -> [XZ_Plane004]
  ExternalBSplineMaxDegree = 5
  ExternalBSplineTolerance = 0.0001
  FullyConstrained = true
  InternalTolerance = 1e-06
  InvalidShape = false
  MakeInternals = false
  MapMode = 5
  Placement = pos=(0,0,0) rot=(1,0,0;1.5708rad)
  Support = -> [XZ_Plane004]
  TreeRank = 94
  ValidateShape = true
  expr: Constraints[16] = <<Parameters>>.m4_shaft_diameter
  sketch-geometry (6):
    g0: LineSegment StartX=-13.1 StartY=0 StartZ=0 EndX=13.1 EndY=0 EndZ=0
    g1: LineSegment StartX=13.1 StartY=0 StartZ=0 EndX=13.1 EndY=25 EndZ=0
    g2: LineSegment StartX=13.1 StartY=25 StartZ=0 EndX=-13.1 EndY=25 EndZ=0
    g3: LineSegment StartX=-13.1 StartY=25 StartZ=0 EndX=-13.1 EndY=0 EndZ=0
    g4: Circle CenterX=0 CenterY=6 CenterZ=0 NormalX=0 NormalY=0 NormalZ=1 AngleXU=0 Radius=2.145
    g5: Circle CenterX=0 CenterY=19 CenterZ=0 NormalX=0 NormalY=0 NormalZ=1 AngleXU=0 Radius=2.145
  constraints (17):
    c: Coincident(g0,g1)
    c: Coincident(g1,g2)
    c: Coincident(g2,g3)
    c: Coincident(g3,g0)
    c: Horizontal(g0)
    c: Horizontal(g2)
    c: Vertical(g1)
    c: Vertical(g3)
    c: DistanceY(g0,g1) = 25
    c: DistanceX(g0,g0) = 26.2
    c: Symmetric(g0,g0,g-1)
    c: PointOnObject(g4,g-2)
    c: PointOnObject(g5,g-2)
    c: DistanceY(g-1,g4) = 6
    c: DistanceY(g-1,g5) = 19
    c: Equal(g5,g4)
    c: Diameter(g5) = 4.29
FEATURE [PartDesign::Pad] Pad006
  AddSubType = 0
  AlongSketchNormal = false
  AutoTaperInnerAngle = true
  CheckUpToFaceLimits = true
  ClaimChildren = false
  Direction = (0,-1,2e-16)
  Fit = 0
  FitJoin = 0
  InnerFit = 0
  InnerFitJoin = 0
  InvalidShape = false
  Length = 15
  Length2 = 100
  Linearize = true
  NewSolid = false
  Profile = -> Sketch023
  Reversed = true
  Suppress = false
  TaperInnerAngle = 0
  TaperInnerAngleRev = 0
  TreeRank = 95
  Type = 0
  ValidateShape = true
  _ProfileBasedVersion = 1
FEATURE [Sketcher::SketchObject] Sketch024
  ArcFitTolerance = 1e-06
  AttachmentSupport = -> [XZ_Plane004]
  ExternalBSplineMaxDegree = 5
  ExternalBSplineTolerance = 0.0001
  FullyConstrained = true
  InternalTolerance = 1e-06
  InvalidShape = false
  MakeInternals = false
  MapMode = 5
  Placement = pos=(0,0,0) rot=(1,0,0;1.5708rad)
  Support = -> [XZ_Plane004]
  TreeRank = 96
  ValidateShape = true
  expr: Constraints[5] = <<Parameters>>.m4_head_diameter
  sketch-geometry (2):
    g0: Circle CenterX=0 CenterY=6 CenterZ=0 NormalX=0 NormalY=0 NormalZ=1 AngleXU=0 Radius=4.4
    g1: Circle CenterX=0 CenterY=19 CenterZ=0 NormalX=0 NormalY=0 NormalZ=1 AngleXU=0 Radius=4.4
  constraints (6):
    c: PointOnObject(g0,g-2)
    c: PointOnObject(g1,g-2)
    c: DistanceY(g-1,g0) = 6
    c: DistanceY(g-1,g1) = 19
    c: Equal(g1,g0)
    c: Diameter(g1) = 8.8
FEATURE [PartDesign::Pocket] Pocket016
  AddSubType = 1
  AutoTaperInnerAngle = true
  BaseFeature = -> Pad006
  CheckUpToFaceLimits = true
  ClaimChildren = false
  Fit = 0
  FitJoin = 0
  InnerFit = 0
  InnerFitJoin = 0
  InvalidShape = false
  Length = 3.25
  Length2 = 100
  Linearize = true
  NewSolid = false
  Profile = -> Sketch024
  Suppress = false
  TaperInnerAngle = 0
  TaperInnerAngleRev = 0
  TreeRank = 97
  Type = 0
  ValidateShape = true
  _ProfileBasedVersion = 1
  _Version = 1
FEATURE [Sketcher::SketchObject] Sketch025
  ArcFitTolerance = 1e-06
  AttachmentOffset = pos=(0,0,13.1) rot=(0,0,1;0rad)
  AttachmentSupport = -> [YZ_Plane004]
  ExternalBSplineMaxDegree = 5
  ExternalBSplineTolerance = 0.0001
  FullyConstrained = true
  InternalTolerance = 1e-06
  InvalidShape = false
  MakeInternals = false
  MapMode = 5
  Placement = pos=(13.1,-2.9e-15,2.9e-15) rot=(0.57735,0.57735,0.57735;2.0944rad)
  Support = -> [YZ_Plane004]
  TreeRank = 98
  ValidateShape = true
  sketch-geometry (7):
    g0: Circle CenterX=7.5 CenterY=18.75 CenterZ=0 NormalX=0 NormalY=0 NormalZ=1 AngleXU=0 Radius=1.25
    g1: Circle CenterX=7.5 CenterY=12.5 CenterZ=0 NormalX=0 NormalY=0 NormalZ=1 AngleXU=0 Radius=1.25
    g2: Circle CenterX=7.5 CenterY=6.25 CenterZ=0 NormalX=0 NormalY=0 NormalZ=1 AngleXU=0 Radius=1.25
    g3: LineSegment [constr] StartX=7.5 StartY=6.25 StartZ=0 EndX=7.5 EndY=12.5 EndZ=0
    g4: LineSegment [constr] StartX=7.5 StartY=12.5 StartZ=0 EndX=7.5 EndY=18.75 EndZ=0
    g5: LineSegment [constr] StartX=7.5 StartY=0 StartZ=0 EndX=7.5 EndY=6.25 EndZ=0
    g6: LineSegment [constr] StartX=7.5 StartY=18.75 StartZ=0 EndX=7.5 EndY=25 EndZ=0
  constraints (19):
    c: DistanceX(g1,g0) = 0
    c: DistanceX(g2,g0) = 0
    c: DistanceX(g-1,g0) = 7.5
    c: Coincident(g3,g2)
    c: Coincident(g3,g1)
    c: Coincident(g4,g1)
    c: Coincident(g4,g0)
    c: PointOnObject(g5,g-1)
    c: Coincident(g5,g2)
    c: Vertical(g5)
    c: Equal(g5,g3)
    c: Equal(g5,g4)
    c: Coincident(g6,g0)
    c: Vertical(g6)
    c: DistanceY(g-1,g6) = 25
    c: Equal(g5,g6)
    c: Equal(g0,g1)
    c: Equal(g0,g2)
    c: Diameter(g0) = 2.5
FEATURE [PartDesign::Hole] Hole002
  AddSubType = 1
  BaseFeature = -> Pocket016
  ClaimChildren = false
  CustomThreadClearance = 0
  Depth = 50
  DepthType = 0
  Diameter = 2.52
  DrillForDepth = false
  DrillPoint = 1
  DrillPointAngle = 118
  Fit = 0
  FitJoin = 0
  HoleCutCountersinkAngle = 90
  HoleCutCustomValues = false
  HoleCutDepth = 0
  HoleCutDiameter = 6.1
  HoleCutType = 0
  InnerFit = 0
  InnerFitJoin = 0
  InvalidShape = false
  Linearize = true
  ModelThread = true
  NewSolid = false
  Profile = -> Sketch025
  Suppress = false
  Tapered = false
  TaperedAngle = 90
  ThreadClass = 0
  ThreadDepth = 50
  ThreadDepthType = 0
  ThreadDirection = 0
  ThreadFit = 0
  ThreadSize = 9
  ThreadType = 1
  Threaded = true
  TreeRank = 99
  UseCustomThreadClearance = false
  ValidateShape = true
  _ProfileBasedVersion = 1
FEATURE [PartDesign::Body] Body004  label="Three Piece - C"
  AutoGroupSolids = false
  ClaimAllChildren = false
  ExportMode = 0
  Group = -> [Sketch023,Pad006,Sketch024,Pocket016,Sketch025,Hole002]
  InvalidShape = false
  Origin = -> Origin004
  Tip = -> Hole002
  TreeRank = 93
  ValidateShape = true
  _ExportChildren = -> [Pad006,Pocket016,Hole002]
  _GroupVersion = 1
FEATURE [Sketcher::SketchObject] Sketch026
  ArcFitTolerance = 1e-06
  AttachmentSupport = -> [XZ_Plane003]
  ExternalBSplineMaxDegree = 5
  ExternalBSplineTolerance = 0.0001
  FullyConstrained = true
  InternalTolerance = 1e-06
  InvalidShape = false
  MakeInternals = false
  MapMode = 5
  Placement = pos=(0,0,0) rot=(1,0,0;1.5708rad)
  Support = -> [XZ_Plane003]
  TreeRank = 100
  ValidateShape = true
  sketch-geometry (5):
    g0: LineSegment StartX=15 StartY=44 StartZ=0 EndX=15 EndY=94 EndZ=0
    g1: LineSegment StartX=15 StartY=94 StartZ=0 EndX=-15 EndY=94 EndZ=0
    g2: LineSegment StartX=-15 StartY=94 StartZ=0 EndX=-15 EndY=44 EndZ=0
    g3: LineSegment StartX=-15 StartY=44 StartZ=0 EndX=15 EndY=44 EndZ=0
    g4: GeomPoint [constr] X=0 Y=69 Z=0
  constraints (13):
    c: Coincident(g0,g1)
    c: Coincident(g1,g2)
    c: Coincident(g2,g3)
    c: Coincident(g3,g0)
    c: Horizontal(g1)
    c: Horizontal(g3)
    c: Vertical(g0)
    c: Vertical(g2)
    c: Symmetric(g1,g0,g4)
    c: PointOnObject(g4,g-2)
    c: DistanceY(g0,g0) = 50
    c: DistanceX(g1,g0) = 30
    c: DistanceY(g-1,g4) = 69
FEATURE [PartDesign::Pocket] Pocket017
  AddSubType = 1
  AutoTaperInnerAngle = true
  BaseFeature = -> Hole001
  CheckUpToFaceLimits = true
  ClaimChildren = false
  Fit = 0
  FitJoin = 0
  InnerFit = 0
  InnerFitJoin = 0
  InvalidShape = false
  Length = 20
  Length2 = 100
  Linearize = true
  NewSolid = false
  Profile = -> Sketch026
  Suppress = false
  TaperInnerAngle = 0
  TaperInnerAngleRev = 0
  TreeRank = 101
  Type = 0
  ValidateShape = true
  _ProfileBasedVersion = 1
  _Version = 1
FEATURE [Sketcher::SketchObject] Sketch027
  ArcFitTolerance = 1e-06
  AttachmentSupport = -> [XY_Plane005]
  ExternalBSplineMaxDegree = 5
  ExternalBSplineTolerance = 0.0001
  FullyConstrained = true
  InternalTolerance = 1e-06
  InvalidShape = false
  MakeInternals = false
  MapMode = 5
  Support = -> [XY_Plane005]
  TreeRank = 112
  ValidateShape = true
  expr: Constraints[27] = <<Parameters>>.m3_shaft_diameter
  sketch-geometry (11):
    g0: LineSegment StartX=-30 StartY=0 StartZ=0 EndX=30 EndY=0 EndZ=0
    g1: LineSegment StartX=30 StartY=0 StartZ=0 EndX=30 EndY=20 EndZ=0
    g2: LineSegment StartX=30 StartY=20 StartZ=0 EndX=-30 EndY=20 EndZ=0
    g3: LineSegment StartX=-30 StartY=20 StartZ=0 EndX=-30 EndY=0 EndZ=0
    g4: Circle CenterX=-8.75 CenterY=12.5 CenterZ=0 NormalX=0 NormalY=0 NormalZ=1 AngleXU=0 Radius=1.595
    g5: Circle CenterX=-2.5 CenterY=12.5 CenterZ=0 NormalX=0 NormalY=0 NormalZ=1 AngleXU=0 Radius=1.595
    g6: Circle CenterX=3.75 CenterY=12.5 CenterZ=0 NormalX=0 NormalY=0 NormalZ=1 AngleXU=0 Radius=1.595
    g7: LineSegment [constr] StartX=-8.75 StartY=12.5 StartZ=0 EndX=-2.5 EndY=12.5 EndZ=0
    g8: LineSegment [constr] StartX=-2.5 StartY=12.5 StartZ=0 EndX=3.75 EndY=12.5 EndZ=0
    g9: LineSegment [constr] StartX=3.75 StartY=12.5 StartZ=0 EndX=10 EndY=12.5 EndZ=0
    g10: LineSegment [constr] StartX=-8.75 StartY=12.5 StartZ=0 EndX=-15 EndY=12.5 EndZ=0
  constraints (30):
    c: Coincident(g0,g1)
    c: Coincident(g1,g2)
    c: Coincident(g2,g3)
    c: Coincident(g3,g0)
    c: Horizontal(g0)
    c: Horizontal(g2)
    c: Vertical(g1)
    c: Vertical(g3)
    c: DistanceX(g0,g0) = 60
    c: Symmetric(g0,g0,g-1)
    c: DistanceY(g0,g1) = 20
    c: Equal(g4,g5)
    c: Equal(g4,g6)
    c: Coincident(g7,g4)
    c: Coincident(g7,g5)
    c: Horizontal(g7)
    c: Coincident(g8,g5)
    c: Coincident(g8,g6)
    c: Horizontal(g8)
    c: Coincident(g9,g6)
    c: Horizontal(g9)
    c: Coincident(g10,g4)
    c: Horizontal(g10)
    c: Equal(g10,g7)
    c: Equal(g10,g8)
    c: Equal(g10,g9)
    c: DistanceX(g10,g9) = 25
    c: Diameter(g4) = 3.19
    c: DistanceX(g9,g0) = 20
    c: DistanceY(g-1,g6) = 12.5
FEATURE [PartDesign::Pad] Pad007
  AddSubType = 0
  AlongSketchNormal = false
  AutoTaperInnerAngle = true
  CheckUpToFaceLimits = true
  ClaimChildren = false
  Direction = (0,0,1)
  Fit = 0
  FitJoin = 0
  InnerFit = 0
  InnerFitJoin = 0
  InvalidShape = false
  Length = 5
  Length2 = 100
  Linearize = true
  NewSolid = false
  Profile = -> Sketch027
  Reversed = true
  Suppress = false
  TaperInnerAngle = 0
  TaperInnerAngleRev = 0
  TreeRank = 113
  Type = 0
  ValidateShape = true
  _ProfileBasedVersion = 1
FEATURE [Sketcher::SketchObject] Sketch028
  ArcFitTolerance = 1e-06
  AttachmentSupport = -> [XY_Plane005]
  ExternalBSplineMaxDegree = 5
  ExternalBSplineTolerance = 0.0001
  FullyConstrained = true
  InternalTolerance = 1e-06
  InvalidShape = false
  MakeInternals = false
  MapMode = 5
  Support = -> [XY_Plane005]
  TreeRank = 114
  ValidateShape = true
  sketch-geometry (8):
    g0: LineSegment StartX=-30 StartY=20 StartZ=0 EndX=-30 EndY=0 EndZ=0
    g1: LineSegment StartX=-30 StartY=0 StartZ=0 EndX=30 EndY=0 EndZ=0
    g2: LineSegment StartX=30 StartY=0 StartZ=0 EndX=30 EndY=20 EndZ=0
    g3: LineSegment StartX=30 StartY=20 StartZ=0 EndX=25.325 EndY=20 EndZ=0
    g4: LineSegment StartX=25.325 StartY=20 StartZ=0 EndX=25.325 EndY=5 EndZ=0
    g5: LineSegment StartX=25.325 StartY=5 StartZ=0 EndX=-25.325 EndY=5 EndZ=0
    g6: LineSegment StartX=-25.325 StartY=5 StartZ=0 EndX=-25.325 EndY=20 EndZ=0
    g7: LineSegment StartX=-25.325 StartY=20 StartZ=0 EndX=-30 EndY=20 EndZ=0
  constraints (23):
    c: PointOnObject(g0,g-1)
    c: Vertical(g0)
    c: Coincident(g1,g0)
    c: Coincident(g2,g1)
    c: Vertical(g2)
    c: Coincident(g3,g2)
    c: Horizontal(g3)
    c: Coincident(g4,g3)
    c: Vertical(g4)
    c: Coincident(g5,g4)
    c: Horizontal(g5)
    c: Coincident(g6,g5)
    c: Vertical(g6)
    c: Coincident(g7,g6)
    c: Coincident(g7,g0)
    c: Horizontal(g7)
    c: Equal(g7,g3)
    c: Equal(g4,g6)
    c: Symmetric(g0,g1,g-1)
    c: DistanceX(g0,g1) = 60
    c: DistanceY(g1,g4) = 5
    c: DistanceX(g5,g4) = 50.65
    c: DistanceY(g1,g2) = 20
FEATURE [PartDesign::Pad] Pad008
  AddSubType = 0
  AlongSketchNormal = false
  AutoTaperInnerAngle = true
  BaseFeature = -> Pad007
  CheckUpToFaceLimits = true
  ClaimChildren = false
  Direction = (0,0,1)
  Fit = 0
  FitJoin = 0
  InnerFit = 0
  InnerFitJoin = 0
  InvalidShape = false
  Length = 0.8
  Length2 = 100
  Linearize = true
  NewSolid = false
  Profile = -> Sketch028
  Suppress = false
  TaperInnerAngle = 0
  TaperInnerAngleRev = 0
  TreeRank = 115
  Type = 0
  ValidateShape = true
  _ProfileBasedVersion = 1
FEATURE [PartDesign::Body] Body005  label="Contact Template"
  AutoGroupSolids = false
  ClaimAllChildren = false
  ExportMode = 0
  Group = -> [Sketch027,Pad007,Sketch028,Pad008]
  InvalidShape = false
  Origin = -> Origin005
  Tip = -> Pad008
  TreeRank = 32
  ValidateShape = true
  _ExportChildren = -> [Pad007,Pad008]
  _GroupVersion = 1
FEATURE [Sketcher::SketchObject] Sketch029
  ArcFitTolerance = 1e-06
  AttachmentSupport = -> [XY_Plane003]
  ExternalBSplineMaxDegree = 5
  ExternalBSplineTolerance = 0.0001
  FullyConstrained = true
  InternalTolerance = 1e-06
  InvalidShape = false
  MakeInternals = false
  MapMode = 5
  Support = -> [XY_Plane003]
  TreeRank = 50
  ValidateShape = true
  expr: Constraints[37] = <<Parameters>>.charger_hole_diameter + 12
  expr: Constraints[38] = <<Parameters>>.charger_offset
  sketch-geometry (14):
    g0: LineSegment StartX=-17.5 StartY=25.7 StartZ=0 EndX=17.5 EndY=25.7 EndZ=0
    g1: LineSegment StartX=-17.5 StartY=25.7 StartZ=0 EndX=-26 EndY=10 EndZ=0
    g2: LineSegment StartX=17.5 StartY=25.7 StartZ=0 EndX=26 EndY=10 EndZ=0
    g3: LineSegment StartX=-26 StartY=10 StartZ=0 EndX=-36 EndY=10 EndZ=0
    g4: LineSegment StartX=26 StartY=10 StartZ=0 EndX=36 EndY=10 EndZ=0
    g5: LineSegment StartX=-36 StartY=10 StartZ=0 EndX=-36 EndY=5 EndZ=0
    g6: LineSegment StartX=-36 StartY=5 StartZ=0 EndX=-26 EndY=5 EndZ=0
    g7: LineSegment StartX=-26 StartY=5 StartZ=0 EndX=-26 EndY=0 EndZ=0
    g8: LineSegment StartX=36 StartY=10 StartZ=0 EndX=36 EndY=5 EndZ=0
    g9: LineSegment StartX=36 StartY=5 StartZ=0 EndX=26 EndY=5 EndZ=0
    g10: LineSegment StartX=26 StartY=5 StartZ=0 EndX=26 EndY=0 EndZ=0
    g11: LineSegment StartX=-26 StartY=0 StartZ=0 EndX=-20.532 EndY=0 EndZ=0
    g12: LineSegment StartX=26 StartY=0 StartZ=0 EndX=20.532 EndY=0 EndZ=0
    g13: ArcOfCircle CenterX=0 CenterY=3 CenterZ=0 NormalX=0 NormalY=0 NormalZ=1 AngleXU=0 Radius=20.75 StartAngle=3.28668 EndAngle=6.1381
  constraints (41):
    c: DistanceX(g0,g0) = 35
    c: Symmetric(g0,g0,g-2)
    c: Coincident(g1,g0)
    c: Coincident(g2,g0)
    c: DistanceY(g2,g0) = 15.7
    c: Symmetric(g1,g2,g-2)
    c: DistanceX(g1,g2) = 52
    c: Coincident(g3,g1)
    c: Horizontal(g3)
    c: Coincident(g4,g2)
    c: Horizontal(g4)
    c: Equal(g3,g4)
    c: DistanceX(g3,g4) = 72
    c: Coincident(g5,g3)
    c: Vertical(g5)
    c: Coincident(g6,g5)
    c: Horizontal(g6)
    c: Coincident(g7,g6)
    c: PointOnObject(g7,g-1)
    c: Vertical(g7)
    c: DistanceY(g5,g3) = 5
    c: DistanceX(g5,g6) = 10
    c: DistanceY(g7,g6) = 5
    c: Coincident(g8,g4)
    c: Vertical(g8)
    c: Coincident(g9,g8)
    c: Horizontal(g9)
    c: Coincident(g10,g9)
    c: PointOnObject(g10,g-1)
    c: Vertical(g10)
    c: Equal(g5,g8)
    c: Equal(g6,g9)
    c: Coincident(g11,g7)
    c: Coincident(g12,g10)
    c: Horizontal(g11)
    c: Horizontal(g12)
    c: PointOnObject(g13,g-2)
    c: Diameter(g13) = 41.5
    c: DistanceY(g13,g-1) = -3
    c: Coincident(g13,g12)
    c: Coincident(g13,g11)
FEATURE [PartDesign::Pad] Pad009
  AddSubType = 0
  AlongSketchNormal = false
  AutoTaperInnerAngle = true
  CheckUpToFaceLimits = true
  ClaimChildren = false
  Direction = (0,0,1)
  Fit = 0
  FitJoin = 0
  InnerFit = 0
  InnerFitJoin = 0
  InvalidShape = false
  Length = 110
  Length2 = 100
  Linearize = true
  NewSolid = false
  Profile = -> Sketch029
  Suppress = false
  TaperInnerAngle = 0
  TaperInnerAngleRev = 0
  TreeRank = 76
  Type = 0
  ValidateShape = true
  _ProfileBasedVersion = 1
FEATURE [Sketcher::SketchObject] Sketch030
  ArcFitTolerance = 1e-06
  AttachmentSupport = -> [XZ_Plane006]
  ExternalBSplineMaxDegree = 5
  ExternalBSplineTolerance = 0.0001
  FullyConstrained = true
  InternalTolerance = 1e-06
  InvalidShape = false
  MakeInternals = false
  MapMode = 5
  Placement = pos=(0,0,0) rot=(1,0,0;1.5708rad)
  Support = -> [XZ_Plane006]
  TreeRank = 56
  ValidateShape = true
  sketch-geometry (18):
    g0: LineSegment StartX=-13.9 StartY=25 StartZ=0 EndX=-22.5 EndY=25 EndZ=0
    g1: LineSegment StartX=13.9 StartY=25 StartZ=0 EndX=22.5 EndY=25 EndZ=0
    g2: LineSegment StartX=-22.5 StartY=25 StartZ=0 EndX=-22.5 EndY=105 EndZ=0
    g3: LineSegment StartX=22.5 StartY=25 StartZ=0 EndX=22.5 EndY=105 EndZ=0
    g4: LineSegment StartX=22.5 StartY=105 StartZ=0 EndX=-22.5 EndY=105 EndZ=0
    g5: LineSegment StartX=-13.9 StartY=0 StartZ=0 EndX=13.9 EndY=-4.2e-15 EndZ=0
    g6: LineSegment StartX=-13.9 StartY=25 StartZ=0 EndX=-13.9 EndY=22 EndZ=0
    g7: LineSegment StartX=-13.9 StartY=22 StartZ=0 EndX=-16.9 EndY=22 EndZ=0
    g8: LineSegment StartX=-16.9 StartY=22 StartZ=0 EndX=-16.9 EndY=12.5 EndZ=0
    g9: LineSegment StartX=-16.9 StartY=12.5 StartZ=0 EndX=-16.9 EndY=3 EndZ=0
    g10: LineSegment StartX=-16.9 StartY=3 StartZ=0 EndX=-13.9 EndY=3 EndZ=0
    g11: LineSegment StartX=-13.9 StartY=3 StartZ=0 EndX=-13.9 EndY=0 EndZ=0
    g12: LineSegment StartX=13.9 StartY=25 StartZ=0 EndX=13.9 EndY=22 EndZ=0
    g13: LineSegment StartX=13.9 StartY=22 StartZ=0 EndX=16.9 EndY=22 EndZ=0
    g14: LineSegment StartX=16.9 StartY=22 StartZ=0 EndX=16.9 EndY=12.5 EndZ=0
    g15: LineSegment StartX=16.9 StartY=12.5 StartZ=0 EndX=16.9 EndY=3 EndZ=0
    g16: LineSegment StartX=16.9 StartY=3 StartZ=0 EndX=13.9 EndY=3 EndZ=0
    g17: LineSegment StartX=13.9 StartY=3 StartZ=0 EndX=13.9 EndY=-4.4e-15 EndZ=0
  constraints (53):
    c: Horizontal(g0)
    c: Horizontal(g1)
    c: Equal(g0,g1)
    c: Coincident(g2,g0)
    c: Vertical(g2)
    c: Coincident(g3,g1)
    c: Vertical(g3)
    c: Coincident(g4,g3)
    c: Coincident(g4,g2)
    c: Horizontal(g4)
    c: DistanceX(g2,g3) = 45
    c: DistanceY(g-1,g3) = 105
    c: PointOnObject(g5,g-1)
    c: DistanceX(g5,g5) = 27.8
    c: Symmetric(g5,g5,g-1)
    c: DistanceY(g5,g1) = 25
    c: Coincident(g6,g0)
    c: Vertical(g6)
    c: Coincident(g7,g6)
    c: Horizontal(g7)
    c: Coincident(g8,g7)
    c: Vertical(g8)
    c: Vertical(g9)
    c: Coincident(g10,g9)
    c: Horizontal(g10)
    c: Coincident(g11,g10)
    c: Coincident(g11,g5)
    c: Vertical(g11)
    c: Coincident(g12,g1)
    c: Vertical(g12)
    c: Coincident(g13,g12)
    c: Horizontal(g13)
    c: Coincident(g14,g13)
    c: Vertical(g14)
    c: Vertical(g15)
    c: Coincident(g16,g15)
    c: Horizontal(g16)
    c: Coincident(g17,g16)
    c: Coincident(g17,g5)
    c: Vertical(g17)
    c: Equal(g8,g9)
    c: Equal(g8,g14)
    c: Equal(g8,g15)
    c: Equal(g7,g10)
    c: Equal(g7,g13)
    c: Equal(g7,g16)
    c: DistanceY(g-1,g0) = 25
    c: Equal(g6,g11)
    c: Equal(g6,g12)
    c: DistanceX(g7,g6) = 3
    c: DistanceY(g5,g10) = 3
    c: Coincident(g9,g8)
    c: Coincident(g14,g15)
FEATURE [PartDesign::Pocket] Pocket018
  AddSubType = 1
  AutoTaperInnerAngle = true
  BaseFeature = -> Pad009
  CheckUpToFaceLimits = true
  ClaimChildren = false
  Fit = 0
  FitJoin = 0
  InnerFit = 0
  InnerFitJoin = 0
  InvalidShape = false
  Length = 15
  Length2 = 100
  Linearize = true
  NewSolid = false
  Profile = -> Sketch030
  Suppress = false
  TaperInnerAngle = 0
  TaperInnerAngleRev = 0
  TreeRank = 119
  Type = 4
  ValidateShape = true
  _ProfileBasedVersion = 1
  _Version = 1
FEATURE [Sketcher::SketchObject] Sketch031
  ArcFitTolerance = 1e-06
  AttachmentSupport = -> [XY_Plane006]
  ExternalBSplineMaxDegree = 5
  ExternalBSplineTolerance = 0.0001
  FullyConstrained = true
  InternalTolerance = 1e-06
  InvalidShape = false
  MakeInternals = false
  MapMode = 5
  Support = -> [XY_Plane006]
  TreeRank = 132
  ValidateShape = true
  sketch-geometry (4):
    g0: LineSegment StartX=-75 StartY=0 StartZ=0 EndX=75 EndY=0 EndZ=0
    g1: LineSegment StartX=75 StartY=0 StartZ=0 EndX=75 EndY=-50 EndZ=0
    g2: LineSegment StartX=75 StartY=-50 StartZ=0 EndX=-75 EndY=-50 EndZ=0
    g3: LineSegment StartX=-75 StartY=-50 StartZ=0 EndX=-75 EndY=0 EndZ=0
  constraints (11):
    c: Coincident(g0,g1)
    c: Coincident(g1,g2)
    c: Coincident(g2,g3)
    c: Coincident(g3,g0)
    c: Horizontal(g0)
    c: Horizontal(g2)
    c: Vertical(g1)
    c: Vertical(g3)
    c: DistanceX(g0,g0) = 150
    c: Symmetric(g0,g0,g-1)
    c: DistanceY(g1,g0) = 50
FEATURE [PartDesign::Pocket] Pocket019
  AddSubType = 1
  AutoTaperInnerAngle = true
  BaseFeature = -> Pocket018
  CheckUpToFaceLimits = true
  ClaimChildren = false
  Fit = 0
  FitJoin = 0
  InnerFit = 0
  InnerFitJoin = 0
  InvalidShape = false
  Length = 105
  Length2 = 100
  Linearize = true
  NewSolid = false
  Profile = -> Sketch031
  Reversed = true
  Suppress = false
  TaperInnerAngle = 0
  TaperInnerAngleRev = 0
  TreeRank = 133
  Type = 0
  ValidateShape = true
  _ProfileBasedVersion = 1
  _Version = 1
FEATURE [Sketcher::SketchObject] Sketch032
  ArcFitTolerance = 1e-06
  AttachmentOffset = pos=(0,0,25) rot=(0,0,1;0rad)
  AttachmentSupport = -> [XY_Plane006]
  ExternalBSplineMaxDegree = 5
  ExternalBSplineTolerance = 0.0001
  FullyConstrained = true
  InternalTolerance = 1e-06
  InvalidShape = false
  MakeInternals = false
  MapMode = 5
  Placement = pos=(0,0,25) rot=(0,0,1;0rad)
  Support = -> [XY_Plane006]
  TreeRank = 134
  ValidateShape = true
  expr: Constraints[0] = <<Parameters>>.charger_hole_diameter + 12
  expr: Constraints[1] = <<Parameters>>.charger_offset
  sketch-geometry (1):
    g0: Circle CenterX=0 CenterY=3 CenterZ=0 NormalX=0 NormalY=0 NormalZ=1 AngleXU=0 Radius=20.75
  constraints (3):
    c: Diameter(g0) = 41.5
    c: DistanceY(g0,g-1) = -3
    c: PointOnObject(g0,g-2)
FEATURE [PartDesign::Pocket] Pocket020
  AddSubType = 1
  AutoTaperInnerAngle = true
  BaseFeature = -> Pocket019
  CheckUpToFaceLimits = true
  ClaimChildren = false
  Fit = 0
  FitJoin = 0
  InnerFit = 0
  InnerFitJoin = 0
  InvalidShape = false
  Length = 80
  Length2 = 100
  Linearize = true
  NewSolid = false
  Profile = -> Sketch032
  Reversed = true
  Suppress = false
  TaperInnerAngle = 0
  TaperInnerAngleRev = 0
  TreeRank = 135
  Type = 0
  ValidateShape = true
  _ProfileBasedVersion = 1
  _Version = 1
FEATURE [Sketcher::SketchObject] Sketch033
  ArcFitTolerance = 1e-06
  AttachmentOffset = pos=(0,0,105) rot=(0,0,1;0rad)
  AttachmentSupport = -> [XY_Plane006]
  ExternalBSplineMaxDegree = 5
  ExternalBSplineTolerance = 0.0001
  FullyConstrained = true
  InternalTolerance = 1e-06
  InvalidShape = false
  MakeInternals = false
  MapMode = 5
  Placement = pos=(0,0,105) rot=(0,0,1;0rad)
  Support = -> [XY_Plane006]
  TreeRank = 136
  ValidateShape = true
  expr: Constraints[0] = <<Parameters>>.charger_hole_diameter
  expr: Constraints[1] = <<Parameters>>.charger_offset
  sketch-geometry (1):
    g0: Circle CenterX=0 CenterY=3 CenterZ=0 NormalX=0 NormalY=0 NormalZ=1 AngleXU=0 Radius=14.75
  constraints (3):
    c: Diameter(g0) = 29.5
    c: DistanceY(g0,g-1) = -3
    c: PointOnObject(g0,g-2)
FEATURE [PartDesign::Pocket] Pocket021
  AddSubType = 1
  AutoTaperInnerAngle = true
  BaseFeature = -> Pocket020
  CheckUpToFaceLimits = true
  ClaimChildren = false
  Fit = 0
  FitJoin = 0
  InnerFit = 0
  InnerFitJoin = 0
  InvalidShape = false
  Length = 5
  Length2 = 100
  Linearize = true
  NewSolid = false
  Profile = -> Sketch033
  Reversed = true
  Suppress = false
  TaperInnerAngle = 0
  TaperInnerAngleRev = 0
  TreeRank = 137
  Type = 0
  ValidateShape = true
  _ProfileBasedVersion = 1
  _Version = 1
FEATURE [Sketcher::SketchObject] Sketch034
  ArcFitTolerance = 1e-06
  AttachmentOffset = pos=(0,0,-10) rot=(0,0,1;0rad)
  AttachmentSupport = -> [XZ_Plane006]
  ExternalBSplineMaxDegree = 5
  ExternalBSplineTolerance = 0.0001
  FullyConstrained = true
  InternalTolerance = 1e-06
  InvalidShape = false
  MakeInternals = false
  MapMode = 5
  Placement = pos=(0,10,-2.2e-15) rot=(1,0,0;1.5708rad)
  Support = -> [XZ_Plane006]
  TreeRank = 52
  ValidateShape = true
  expr: Constraints[6] = 110 - 37
  expr: Constraints[8] = <<Parameters>>.m4_head_diameter
  sketch-geometry (4):
    g0: Circle CenterX=31 CenterY=73 CenterZ=0 NormalX=0 NormalY=0 NormalZ=1 AngleXU=0 Radius=4.4
    g1: Circle CenterX=31 CenterY=37 CenterZ=0 NormalX=0 NormalY=0 NormalZ=1 AngleXU=0 Radius=4.4
    g2: Circle CenterX=-31 CenterY=37 CenterZ=0 NormalX=0 NormalY=0 NormalZ=1 AngleXU=0 Radius=4.4
    g3: Circle CenterX=-31 CenterY=73 CenterZ=0 NormalX=0 NormalY=0 NormalZ=1 AngleXU=0 Radius=4.4
  constraints (10):
    c: Equal(g0,g3)
    c: Equal(g0,g1)
    c: Equal(g0,g2)
    c: Symmetric(g0,g3,g-2)
    c: Symmetric(g1,g2,g-2)
    c: DistanceY(g-1,g1) = 37
    c: DistanceY(g-1,g0) = 73
    c: DistanceX(g3,g0) = 62
    c: Diameter(g3) = 8.8
    c: DistanceX(g2,g3) = 0
FEATURE [PartDesign::Pocket] Pocket022
  AddSubType = 1
  AutoTaperInnerAngle = true
  BaseFeature = -> Pocket021
  CheckUpToFaceLimits = true
  ClaimChildren = false
  Fit = 0
  FitJoin = 0
  InnerFit = 0
  InnerFitJoin = 0
  InvalidShape = false
  Length = 3
  Length2 = 100
  Linearize = true
  NewSolid = false
  Profile = -> Sketch034
  Reversed = true
  Suppress = false
  TaperInnerAngle = 0
  TaperInnerAngleRev = 0
  TreeRank = 138
  Type = 0
  ValidateShape = true
  _ProfileBasedVersion = 1
  _Version = 1
  expr: Length = <<Parameters>>.screw_head_height
FEATURE [Sketcher::SketchObject] Sketch035
  ArcFitTolerance = 1e-06
  AttachmentOffset = pos=(0,0,-10) rot=(0,0,1;0rad)
  AttachmentSupport = -> [XZ_Plane006]
  ExternalBSplineMaxDegree = 5
  ExternalBSplineTolerance = 0.0001
  FullyConstrained = true
  InternalTolerance = 1e-06
  InvalidShape = false
  MakeInternals = false
  MapMode = 5
  Placement = pos=(0,10,-2.2e-15) rot=(1,0,0;1.5708rad)
  Support = -> [XZ_Plane006]
  TreeRank = 54
  ValidateShape = true
  expr: Constraints[6] = 110 - 37
  expr: Constraints[8] = <<Parameters>>.m4_shaft_diameter
  sketch-geometry (4):
    g0: Circle CenterX=31 CenterY=73 CenterZ=0 NormalX=0 NormalY=0 NormalZ=1 AngleXU=0 Radius=2.145
    g1: Circle CenterX=31 CenterY=37 CenterZ=0 NormalX=0 NormalY=0 NormalZ=1 AngleXU=0 Radius=2.145
    g2: Circle CenterX=-31 CenterY=37 CenterZ=0 NormalX=0 NormalY=0 NormalZ=1 AngleXU=0 Radius=2.145
    g3: Circle CenterX=-31 CenterY=73 CenterZ=0 NormalX=0 NormalY=0 NormalZ=1 AngleXU=0 Radius=2.145
  constraints (10):
    c: Equal(g0,g3)
    c: Equal(g0,g1)
    c: Equal(g0,g2)
    c: Symmetric(g0,g3,g-2)
    c: Symmetric(g1,g2,g-2)
    c: DistanceY(g-1,g1) = 37
    c: DistanceY(g-1,g0) = 73
    c: DistanceX(g3,g0) = 62
    c: Diameter(g3) = 4.29
    c: DistanceX(g2,g3) = 0
FEATURE [PartDesign::Pocket] Pocket023
  AddSubType = 1
  AutoTaperInnerAngle = true
  BaseFeature = -> Pocket022
  CheckUpToFaceLimits = true
  ClaimChildren = false
  Fit = 0
  FitJoin = 0
  InnerFit = 0
  InnerFitJoin = 0
  InvalidShape = false
  Length = 5
  Length2 = 100
  Linearize = true
  NewSolid = false
  Profile = -> Sketch035
  Reversed = true
  Suppress = false
  TaperInnerAngle = 0
  TaperInnerAngleRev = 0
  TreeRank = 139
  Type = 0
  ValidateShape = true
  _ProfileBasedVersion = 1
  _Version = 1
FEATURE [Sketcher::SketchObject] Sketch036
  ArcFitTolerance = 1e-06
  AttachmentSupport = -> [XY_Plane007]
  ExternalBSplineMaxDegree = 5
  ExternalBSplineTolerance = 0.0001
  FullyConstrained = true
  InternalTolerance = 1e-06
  InvalidShape = false
  MakeInternals = false
  MapMode = 5
  Support = -> [XY_Plane007]
  TreeRank = 34
  ValidateShape = true
  expr: Constraints[45] = <<Parameters>>.charger_hole_diameter + 12 + 2 * <<Parameters>>.thickness
  expr: Constraints[50] = -<<Parameters>>.charger_offset
  sketch-geometry (19):
    g0: LineSegment StartX=-36 StartY=10 StartZ=0 EndX=-45 EndY=10 EndZ=0
    g1: LineSegment StartX=36 StartY=10 StartZ=0 EndX=45 EndY=10 EndZ=0
    g2: LineSegment StartX=-41 StartY=-6 StartZ=0 EndX=-21.9787 EndY=-6 EndZ=0
    g3: LineSegment StartX=-45 StartY=10 StartZ=0 EndX=-45 EndY=0 EndZ=0
    g4: LineSegment StartX=-45 StartY=1e-16 StartZ=0 EndX=-41 EndY=1e-16 EndZ=0
    g5: LineSegment StartX=-41 StartY=-6 StartZ=0 EndX=-41 EndY=0 EndZ=0
    g6: LineSegment StartX=45 StartY=10 StartZ=0 EndX=45 EndY=0 EndZ=0
    g7: LineSegment StartX=45 StartY=0 StartZ=0 EndX=41 EndY=0 EndZ=0
    g8: LineSegment StartX=41 StartY=-6 StartZ=0 EndX=41 EndY=0 EndZ=0
    g9: LineSegment StartX=-26 StartY=0 StartZ=0 EndX=0 EndY=0 EndZ=0
    g10: LineSegment StartX=-26 StartY=0 StartZ=0 EndX=-26 EndY=5 EndZ=0
    g11: LineSegment StartX=26 StartY=0 StartZ=0 EndX=26 EndY=5 EndZ=0
    g12: LineSegment StartX=-26 StartY=5 StartZ=0 EndX=-36 EndY=5 EndZ=0
    g13: LineSegment StartX=-36 StartY=5 StartZ=0 EndX=-36 EndY=10 EndZ=0
    g14: LineSegment StartX=26 StartY=5 StartZ=0 EndX=36 EndY=5 EndZ=0
    g15: LineSegment StartX=36 StartY=5 StartZ=0 EndX=36 EndY=10 EndZ=0
    g16: ArcOfCircle CenterX=0 CenterY=3 CenterZ=0 NormalX=0 NormalY=0 NormalZ=1 AngleXU=0 Radius=23.75 StartAngle=3.53025 EndAngle=5.89453
    g17: LineSegment StartX=21.9787 StartY=-6 StartZ=0 EndX=41 EndY=-6 EndZ=0
    g18: LineSegment StartX=0 StartY=0 StartZ=0 EndX=26 EndY=0 EndZ=0
  constraints (54):
    c: Symmetric(g0,g1,g-2)
    c: DistanceX(g0,g1) = 72
    c: Horizontal(g0)
    c: Horizontal(g1)
    c: Equal(g0,g1)
    c: DistanceY(g17,g1) = 16
    c: DistanceX(g0,g1) = 90
    c: DistanceX(g2,g17) = 82
    c: Coincident(g3,g0)
    c: Vertical(g3)
    c: Coincident(g4,g3)
    c: Horizontal(g4)
    c: Coincident(g5,g2)
    c: Coincident(g5,g4)
    c: Vertical(g5)
    c: Coincident(g6,g1)
    c: Vertical(g6)
    c: Coincident(g7,g6)
    c: Horizontal(g7)
    c: Coincident(g8,g17)
    c: Coincident(g8,g7)
    c: Vertical(g8)
    c: Equal(g3,g6)
    c: DistanceY(g6,g1) = 10
    c: PointOnObject(g7,g-1)
    c: PointOnObject(g9,g-1)
    c: Coincident(g10,g9)
    c: Vertical(g10)
    c: DistanceY(g9,g10) = 5
    c: Coincident(g11,g18)
    c: Vertical(g11)
    c: Equal(g10,g11)
    c: Symmetric(g9,g18,g-1)
    c: Coincident(g12,g10)
    c: Horizontal(g12)
    c: Coincident(g13,g12)
    c: Coincident(g13,g0)
    c: Vertical(g13)
    c: Coincident(g14,g11)
    c: Horizontal(g14)
    c: Coincident(g15,g14)
    c: Coincident(g15,g1)
    c: Vertical(g15)
    c: DistanceX(g9,g18) = 52
    c: Symmetric(g2,g17,g-2)
    c: Diameter(g16) = 47.5
    c: Coincident(g16,g2)
    c: Coincident(g16,g17)
    c: Coincident(g18,g9)
    c: PointOnObject(g16,g-2)
    c: DistanceY(g-1,g16) = 3
    c: Horizontal(g17)
    c: Horizontal(g2)
    c: Coincident(g9,g-1)
FEATURE [PartDesign::Pad] Pad010
  AddSubType = 0
  AlongSketchNormal = false
  AutoTaperInnerAngle = true
  CheckUpToFaceLimits = true
  ClaimChildren = false
  Direction = (0,0,1)
  Fit = 0
  FitJoin = 0
  InnerFit = 0
  InnerFitJoin = 0
  InvalidShape = false
  Length = 110
  Length2 = 100
  Linearize = true
  NewSolid = false
  Profile = -> Sketch036
  Suppress = false
  TaperInnerAngle = 0
  TaperInnerAngleRev = 0
  TreeRank = 149
  Type = 0
  ValidateShape = true
  _ProfileBasedVersion = 1
FEATURE [Sketcher::SketchObject] Sketch037
  ArcFitTolerance = 1e-06
  AttachmentOffset = pos=(0,0,25) rot=(0,0,1;0rad)
  AttachmentSupport = -> [XY_Plane007]
  ExternalBSplineMaxDegree = 5
  ExternalBSplineTolerance = 0.0001
  FullyConstrained = true
  InternalTolerance = 1e-06
  InvalidShape = false
  MakeInternals = false
  MapMode = 5
  Placement = pos=(0,0,25) rot=(0,0,1;0rad)
  Support = -> [XY_Plane007]
  TreeRank = 134
  ValidateShape = true
  expr: Constraints[0] = <<Parameters>>.charger_hole_diameter + 12
  expr: Constraints[1] = <<Parameters>>.charger_offset
  sketch-geometry (1):
    g0: Circle CenterX=0 CenterY=3 CenterZ=0 NormalX=0 NormalY=0 NormalZ=1 AngleXU=0 Radius=20.75
  constraints (3):
    c: Diameter(g0) = 41.5
    c: DistanceY(g0,g-1) = -3
    c: PointOnObject(g0,g-2)
FEATURE [PartDesign::Pocket] Pocket024
  AddSubType = 1
  AutoTaperInnerAngle = true
  BaseFeature = -> Pad010
  CheckUpToFaceLimits = true
  ClaimChildren = false
  Fit = 0
  FitJoin = 0
  InnerFit = 0
  InnerFitJoin = 0
  InvalidShape = false
  Length = 100
  Length2 = 100
  Linearize = true
  NewSolid = false
  Profile = -> Sketch037
  Reversed = true
  Suppress = false
  TaperInnerAngle = 0
  TaperInnerAngleRev = 0
  TreeRank = 150
  Type = 0
  ValidateShape = true
  _ProfileBasedVersion = 1
  _Version = 1
FEATURE [Sketcher::SketchObject] Sketch039
  ArcFitTolerance = 1e-06
  AttachmentOffset = pos=(0,0,-45) rot=(0,0,1;0rad)
  AttachmentSupport = -> [YZ_Plane007]
  ExternalBSplineMaxDegree = 5
  ExternalBSplineTolerance = 0.0001
  FullyConstrained = true
  InternalTolerance = 1e-06
  InvalidShape = false
  MakeInternals = false
  MapMode = 5
  Placement = pos=(-45,1e-14,-1e-14) rot=(0.57735,0.57735,0.57735;2.0944rad)
  Support = -> [YZ_Plane007]
  TreeRank = 15
  ValidateShape = true
  sketch-geometry (6):
    g0: LineSegment StartX=2.5 StartY=5 StartZ=0 EndX=10 EndY=5 EndZ=0
    g1: LineSegment StartX=0 StartY=0 StartZ=0 EndX=10 EndY=0 EndZ=0
    g2: LineSegment StartX=10 StartY=5 StartZ=0 EndX=10 EndY=0 EndZ=0
    g3: LineSegment StartX=2.5 StartY=5 StartZ=0 EndX=2.5 EndY=52.5 EndZ=0
    g4: LineSegment StartX=2.5 StartY=52.5 StartZ=0 EndX=0 EndY=57.5 EndZ=0
    g5: LineSegment StartX=0 StartY=57.5 StartZ=0 EndX=0 EndY=0 EndZ=0
  constraints (17):
    c: Horizontal(g0)
    c: DistanceY(g-1,g0) = 5
    c: Coincident(g1,g-1)
    c: PointOnObject(g1,g-1)
    c: Coincident(g2,g0)
    c: Coincident(g2,g1)
    c: Vertical(g2)
    c: DistanceX(g1,g1) = 10
    c: Coincident(g3,g0)
    c: Vertical(g3)
    c: DistanceY(g1,g3) = 52.5
    c: Coincident(g4,g3)
    c: PointOnObject(g4,g-2)
    c: DistanceY(g3,g4) = 5
    c: Coincident(g5,g4)
    c: Coincident(g5,g1)
    c: DistanceX(g1,g0) = 2.5
FEATURE [PartDesign::Pocket] Pocket026
  AddSubType = 1
  AutoTaperInnerAngle = true
  BaseFeature = -> Pocket024
  CheckUpToFaceLimits = true
  ClaimChildren = false
  Fit = 0
  FitJoin = 0
  InnerFit = 0
  InnerFitJoin = 0
  InvalidShape = false
  Length = 4
  Length2 = 100
  Linearize = true
  NewSolid = false
  Profile = -> Sketch039
  Reversed = true
  Suppress = false
  TaperInnerAngle = 0
  TaperInnerAngleRev = 0
  TreeRank = 152
  Type = 0
  ValidateShape = true
  _ProfileBasedVersion = 1
  _Version = 1
FEATURE [Sketcher::SketchObject] Sketch040
  ArcFitTolerance = 1e-06
  AttachmentOffset = pos=(0,0,45) rot=(0,0,1;0rad)
  AttachmentSupport = -> [YZ_Plane007]
  ExternalBSplineMaxDegree = 5
  ExternalBSplineTolerance = 0.0001
  FullyConstrained = true
  InternalTolerance = 1e-06
  InvalidShape = false
  MakeInternals = false
  MapMode = 5
  Placement = pos=(45,-1e-14,1e-14) rot=(0.57735,0.57735,0.57735;2.0944rad)
  Support = -> [YZ_Plane007]
  TreeRank = 17
  ValidateShape = true
  sketch-geometry (6):
    g0: LineSegment StartX=2.5 StartY=5 StartZ=0 EndX=10 EndY=5 EndZ=0
    g1: LineSegment StartX=0 StartY=0 StartZ=0 EndX=10 EndY=0 EndZ=0
    g2: LineSegment StartX=10 StartY=5 StartZ=0 EndX=10 EndY=0 EndZ=0
    g3: LineSegment StartX=2.5 StartY=5 StartZ=0 EndX=2.5 EndY=52.5 EndZ=0
    g4: LineSegment StartX=2.5 StartY=52.5 StartZ=0 EndX=0 EndY=57.5 EndZ=0
    g5: LineSegment StartX=0 StartY=57.5 StartZ=0 EndX=0 EndY=0 EndZ=0
  constraints (17):
    c: Horizontal(g0)
    c: DistanceY(g-1,g0) = 5
    c: Coincident(g1,g-1)
    c: PointOnObject(g1,g-1)
    c: Coincident(g2,g0)
    c: Coincident(g2,g1)
    c: Vertical(g2)
    c: DistanceX(g1,g1) = 10
    c: Coincident(g3,g0)
    c: Vertical(g3)
    c: DistanceY(g1,g3) = 52.5
    c: Coincident(g4,g3)
    c: PointOnObject(g4,g-2)
    c: DistanceY(g3,g4) = 5
    c: Coincident(g5,g4)
    c: Coincident(g5,g1)
    c: DistanceX(g1,g0) = 2.5
FEATURE [PartDesign::Pocket] Pocket027
  AddSubType = 1
  AutoTaperInnerAngle = true
  BaseFeature = -> Pocket026
  CheckUpToFaceLimits = true
  ClaimChildren = false
  Fit = 0
  FitJoin = 0
  InnerFit = 0
  InnerFitJoin = 0
  InvalidShape = false
  Length = 4
  Length2 = 100
  Linearize = true
  NewSolid = false
  Profile = -> Sketch040
  Suppress = false
  TaperInnerAngle = 0
  TaperInnerAngleRev = 0
  TreeRank = 153
  Type = 0
  ValidateShape = true
  _ProfileBasedVersion = 1
  _Version = 1
FEATURE [Sketcher::SketchObject] Sketch041
  ArcFitTolerance = 1e-06
  AttachmentOffset = pos=(0,0,-10) rot=(0,0,1;0rad)
  AttachmentSupport = -> [XZ_Plane007]
  ExternalBSplineMaxDegree = 5
  ExternalBSplineTolerance = 0.0001
  FullyConstrained = false
  InternalTolerance = 1e-06
  InvalidShape = false
  MakeInternals = false
  MapMode = 5
  Placement = pos=(0,10,-2.2e-15) rot=(1,0,0;1.5708rad)
  Support = -> [XZ_Plane007]
  TreeRank = 38
  ValidateShape = true
  expr: Constraints[6] = 110 - 37
  sketch-geometry (4):
    g0: Circle CenterX=31 CenterY=73 CenterZ=0 NormalX=0 NormalY=0 NormalZ=1 AngleXU=0 Radius=2.68754
    g1: Circle CenterX=31 CenterY=37 CenterZ=0 NormalX=0 NormalY=0 NormalZ=1 AngleXU=0 Radius=2.68754
    g2: Circle CenterX=-31 CenterY=37 CenterZ=0 NormalX=0 NormalY=0 NormalZ=1 AngleXU=0 Radius=2.68754
    g3: Circle CenterX=-31 CenterY=73 CenterZ=0 NormalX=0 NormalY=0 NormalZ=1 AngleXU=0 Radius=2.68754
  constraints (9):
    c: Equal(g0,g3)
    c: Equal(g0,g1)
    c: Equal(g0,g2)
    c: Symmetric(g0,g3,g-2)
    c: Symmetric(g1,g2,g-2)
    c: DistanceY(g-1,g1) = 37
    c: DistanceY(g-1,g0) = 73
    c: DistanceX(g3,g0) = 62
    c: DistanceX(g2,g3) = 0
FEATURE [PartDesign::Hole] Hole003
  AddSubType = 1
  BaseFeature = -> Pocket027
  ClaimChildren = false
  CustomThreadClearance = 0
  Depth = 12
  DepthType = 0
  Diameter = 3.322
  DrillForDepth = false
  DrillPoint = 1
  DrillPointAngle = 118
  Fit = 0
  FitJoin = 0
  HoleCutCountersinkAngle = 90
  HoleCutCustomValues = false
  HoleCutDepth = 0
  HoleCutDiameter = 6.1
  HoleCutType = 0
  InnerFit = 0
  InnerFitJoin = 0
  InvalidShape = false
  Linearize = true
  ModelThread = true
  NewSolid = false
  Profile = -> Sketch041
  Reversed = true
  Suppress = false
  Tapered = false
  TaperedAngle = 90
  ThreadClass = 0
  ThreadDepth = 12
  ThreadDepthType = 0
  ThreadDirection = 0
  ThreadFit = 0
  ThreadSize = 11
  ThreadType = 1
  Threaded = true
  TreeRank = 154
  UseCustomThreadClearance = false
  ValidateShape = true
  _ProfileBasedVersion = 1
FEATURE [PartDesign::Chamfer] Chamfer
  AddSubType = 0
  Angle = 45
  Base = -> Hole003 [Edge31]
  BaseFeature = -> Hole003
  ChamferType = 0
  FlipDirection = false
  InvalidShape = false
  NewSolid = false
  Size = 14.2
  Size2 = 1
  SupportTransform = false
  Suppress = false
  TreeRank = 155
  ValidateShape = true
FEATURE [Sketcher::SketchObject] Sketch042
  ArcFitTolerance = 1e-06
  AttachmentSupport = -> [XZ_Plane007]
  ExternalBSplineMaxDegree = 5
  ExternalBSplineTolerance = 0.0001
  FullyConstrained = true
  InternalTolerance = 1e-06
  InvalidShape = false
  MakeInternals = false
  MapMode = 5
  Placement = pos=(0,0,0) rot=(1,0,0;1.5708rad)
  Support = -> [XZ_Plane007]
  TreeRank = 156
  ValidateShape = true
  sketch-geometry (4):
    g0: LineSegment StartX=-41 StartY=0 StartZ=0 EndX=41 EndY=0 EndZ=0
    g1: LineSegment StartX=41 StartY=0 StartZ=0 EndX=41 EndY=-20 EndZ=0
    g2: LineSegment StartX=41 StartY=-20 StartZ=0 EndX=-41 EndY=-20 EndZ=0
    g3: LineSegment StartX=-41 StartY=-20 StartZ=0 EndX=-41 EndY=0 EndZ=0
  constraints (11):
    c: Coincident(g0,g1)
    c: Coincident(g1,g2)
    c: Coincident(g2,g3)
    c: Coincident(g3,g0)
    c: Horizontal(g0)
    c: Horizontal(g2)
    c: Vertical(g1)
    c: Vertical(g3)
    c: DistanceY(g1,g0) = 20
    c: DistanceX(g0,g0) = 82
    c: Symmetric(g0,g0,g-1)
FEATURE [PartDesign::Pad] Pad011
  AddSubType = 0
  AlongSketchNormal = false
  AutoTaperInnerAngle = true
  BaseFeature = -> Chamfer
  CheckUpToFaceLimits = true
  ClaimChildren = false
  Direction = (0,-1,2e-16)
  Fit = 0
  FitJoin = 0
  FixShape = 1
  InnerFit = 0
  InnerFitJoin = 0
  InvalidShape = false
  Length = 6
  Length2 = 100
  Linearize = true
  NewSolid = false
  Profile = -> Sketch042
  Suppress = false
  TaperInnerAngle = 0
  TaperInnerAngleRev = 0
  TreeRank = 157
  Type = 0
  ValidateShape = true
  _ProfileBasedVersion = 1
FEATURE [PartDesign::Chamfer] Chamfer001
  AddSubType = 0
  Angle = 45
  Base = -> Pad011 [Edge25,Edge21]
  BaseFeature = -> Pad011
  ChamferType = 0
  FlipDirection = false
  InvalidShape = false
  NewSolid = false
  Size = 5.99
  Size2 = 1
  SupportTransform = false
  Suppress = false
  TreeRank = 158
  ValidateShape = true
FEATURE [Sketcher::SketchObject] Sketch043
  ArcFitTolerance = 1e-06
  AttachmentOffset = pos=(0,0,20) rot=(0,0,1;0rad)
  AttachmentSupport = -> [XY_Plane007]
  ExternalBSplineMaxDegree = 5
  ExternalBSplineTolerance = 0.0001
  FullyConstrained = false
  InternalTolerance = 1e-06
  InvalidShape = false
  MakeInternals = false
  MapMode = 5
  Placement = pos=(0,0,20) rot=(0,0,1;0rad)
  Support = -> [XY_Plane007]
  TreeRank = 159
  ValidateShape = true
  sketch-geometry (2):
    g0: Circle CenterX=-31.1368 CenterY=-6.00893 CenterZ=0 NormalX=0 NormalY=0 NormalZ=1 AngleXU=0 Radius=7.5
    g1: Circle CenterX=31.1368 CenterY=-6.00893 CenterZ=0 NormalX=0 NormalY=0 NormalZ=1 AngleXU=0 Radius=7.5
  constraints (3):
    c: Equal(g0,g1)
    c: Symmetric(g0,g1,g-2)
    c: Diameter(g0) = 15
FEATURE [PartDesign::Pad] Pad012
  AddSubType = 0
  AlongSketchNormal = false
  AutoTaperInnerAngle = true
  BaseFeature = -> Chamfer001
  CheckUpToFaceLimits = true
  ClaimChildren = false
  Direction = (0,0,1)
  Fit = 0
  FitJoin = 0
  InnerFit = 0
  InnerFitJoin = 0
  InvalidShape = false
  Length = 27
  Length2 = 100
  Linearize = true
  NewSolid = false
  Profile = -> Sketch043
  Suppress = false
  TaperAngle = -15
  TaperInnerAngle = 15
  TaperInnerAngleRev = 0
  TreeRank = 160
  Type = 0
  ValidateShape = true
  _ProfileBasedVersion = 1
FEATURE [PartDesign::Fillet] Fillet
  AddSubType = 0
  Base = -> Pad012 [Edge138,Edge106]
  BaseFeature = -> Pad012
  InvalidShape = false
  NewSolid = false
  Radius = 1
  SupportTransform = false
  Suppress = false
  TreeRank = 161
  ValidateShape = true
FEATURE [PartDesign::Body] Body007  label="Integrated Charger - A"
  AutoGroupSolids = false
  ClaimAllChildren = false
  ExportMode = 0
  Group = -> [Pad010,Sketch036,Pocket024,Sketch037,Pocket026,Pocket027,Sketch039,Sketch040,Hole003,Chamfer,Sketch041,Sketch042,Pad011,Chamfer001,Sketch043,Pad012,Fillet]
  InvalidShape = false
  Origin = -> Origin007
  Tip = -> Fillet
  TreeRank = 117
  ValidateShape = true
  _ExportChildren = -> [Pad010,Pocket024,Pocket026,Pocket027,Hole003,Chamfer,Pad011,Chamfer001,Pad012,Fillet]
  _GroupVersion = 1
FEATURE [Sketcher::SketchObject] Sketch044
  ArcFitTolerance = 1e-06
  AttachmentSupport = -> [XZ_Plane006]
  ExternalBSplineMaxDegree = 5
  ExternalBSplineTolerance = 0.0001
  FullyConstrained = false
  InternalTolerance = 1e-06
  InvalidShape = false
  MakeInternals = false
  MapMode = 5
  Placement = pos=(0,0,0) rot=(1,0,0;1.5708rad)
  Support = -> [XZ_Plane006]
  TreeRank = 82
  ValidateShape = true
  sketch-geometry (2):
    g0: Circle CenterX=0 CenterY=19 CenterZ=0 NormalX=0 NormalY=0 NormalZ=1 AngleXU=0 Radius=1.85369
    g1: Circle CenterX=0 CenterY=6 CenterZ=0 NormalX=0 NormalY=0 NormalZ=1 AngleXU=0 Radius=1.85369
  constraints (5):
    c: PointOnObject(g0,g-2)
    c: PointOnObject(g1,g-2)
    c: Equal(g0,g1)
    c: DistanceY(g-1,g1) = 6
    c: DistanceY(g-1,g0) = 19
FEATURE [PartDesign::Hole] Hole004
  AddSubType = 1
  BaseFeature = -> Pocket023
  ClaimChildren = false
  CustomThreadClearance = 0
  Depth = 24.5
  DepthType = 0
  Diameter = 3.322
  DrillForDepth = false
  DrillPoint = 0
  DrillPointAngle = 118
  Fit = 0
  FitJoin = 0
  HoleCutCountersinkAngle = 90
  HoleCutCustomValues = false
  HoleCutDepth = 0
  HoleCutDiameter = 6.1
  HoleCutType = 0
  InnerFit = 0
  InnerFitJoin = 0
  InvalidShape = false
  Linearize = true
  ModelThread = true
  NewSolid = false
  Profile = -> Sketch044
  Suppress = false
  Tapered = false
  TaperedAngle = 90
  ThreadClass = 0
  ThreadDepth = 24.5
  ThreadDepthType = 0
  ThreadDirection = 0
  ThreadFit = 0
  ThreadSize = 11
  ThreadType = 1
  Threaded = true
  TreeRank = 162
  UseCustomThreadClearance = false
  ValidateShape = true
  _ProfileBasedVersion = 1
FEATURE [PartDesign::Body] Body006  label="Integrated Charger - B"
  AutoGroupSolids = false
  ClaimAllChildren = false
  ExportMode = 0
  Group = -> [Pad009,Sketch029,Pocket018,Sketch030,Sketch031,Pocket019,Sketch032,Pocket020,Sketch033,Pocket021,Pocket022,Pocket023,Sketch034,Sketch035,Hole004,Sketch044]
  InvalidShape = false
  Origin = -> Origin006
  Tip = -> Hole004
  TreeRank = 118
  ValidateShape = true
  _ExportChildren = -> [Pad009,Pocket018,Pocket019,Pocket020,Pocket021,Pocket022,Pocket023,Hole004]
  _GroupVersion = 1
FEATURE [PartDesign::Hole] Hole005
  AddSubType = 1
  BaseFeature = -> Pocket017
  ClaimChildren = false
  CustomThreadClearance = 0
  Depth = 10
  DepthType = 0
  Diameter = 2.52
  DrillForDepth = false
  DrillPoint = 0
  DrillPointAngle = 118
  Fit = 0
  FitJoin = 0
  HoleCutCountersinkAngle = 90
  HoleCutCustomValues = false
  HoleCutDepth = 0
  HoleCutDiameter = 6.1
  HoleCutType = 0
  InnerFit = 0
  InnerFitJoin = 0
  InvalidShape = false
  Linearize = true
  ModelThread = true
  NewSolid = false
  Profile = -> Sketch021
  Suppress = false
  Tapered = false
  TaperedAngle = 90
  ThreadClass = 0
  ThreadDepth = 10
  ThreadDepthType = 0
  ThreadDirection = 0
  ThreadFit = 0
  ThreadSize = 9
  ThreadType = 1
  Threaded = true
  TreeRank = 163
  UseCustomThreadClearance = false
  ValidateShape = true
  _ProfileBasedVersion = 1
FEATURE [Sketcher::SketchObject] Sketch045
  ArcFitTolerance = 1e-06
  AttachmentSupport = -> [XZ_Plane003]
  ExternalBSplineMaxDegree = 5
  ExternalBSplineTolerance = 0.0001
  FullyConstrained = true
  InternalTolerance = 1e-06
  InvalidShape = false
  MakeInternals = false
  MapMode = 5
  Placement = pos=(0,0,0) rot=(1,0,0;1.5708rad)
  Support = -> [XZ_Plane003]
  TreeRank = 164
  ValidateShape = true
  sketch-geometry (4):
    g0: Circle CenterX=0 CenterY=83 CenterZ=0 NormalX=0 NormalY=0 NormalZ=1 AngleXU=0 Radius=4
    g1: Circle CenterX=0 CenterY=55 CenterZ=0 NormalX=0 NormalY=0 NormalZ=1 AngleXU=0 Radius=4
    g2: Circle CenterX=0 CenterY=55 CenterZ=0 NormalX=0 NormalY=0 NormalZ=1 AngleXU=0 Radius=8
    g3: Circle CenterX=0 CenterY=83 CenterZ=0 NormalX=0 NormalY=0 NormalZ=1 AngleXU=0 Radius=8
  constraints (10):
    c: PointOnObject(g0,g-2)
    c: PointOnObject(g1,g-2)
    c: Coincident(g2,g1)
    c: Coincident(g3,g0)
    c: DistanceY(g-1,g1) = 55
    c: DistanceY(g1,g0) = 28
    c: Equal(g0,g1)
    c: Equal(g3,g2)
    c: Diameter(g0) = 8
    c: Diameter(g3) = 16
FEATURE [PartDesign::Pocket] Pocket028
  AddSubType = 1
  AutoTaperInnerAngle = true
  BaseFeature = -> Hole005
  CheckUpToFaceLimits = true
  ClaimChildren = false
  Fit = 0
  FitJoin = 0
  InnerFit = 0
  InnerFitJoin = 0
  InvalidShape = false
  Length = 23
  Length2 = 100
  Linearize = true
  NewSolid = false
  Profile = -> Sketch045
  Suppress = false
  TaperInnerAngle = 0
  TaperInnerAngleRev = 0
  TreeRank = 165
  Type = 0
  ValidateShape = true
  _ProfileBasedVersion = 1
  _Version = 1
FEATURE [PartDesign::Body] Body003  label="Three Piece - B"
  AutoGroupSolids = false
  ClaimAllChildren = false
  ExportMode = 0
  Group = -> [Pad004,Sketch016,Pocket012,Pocket013,Pocket014,Sketch018,Sketch019,Sketch020,Sketch021,Sketch022,Hole001,Sketch026,Pocket017,Hole005,Sketch045,Pocket028]
  InvalidShape = false
  Origin = -> Origin003
  Tip = -> Pocket028
  TreeRank = 75
  ValidateShape = true
  _ExportChildren = -> [Pad004,Pocket012,Pocket013,Pocket014,Hole001,Pocket017,Hole005,Pocket028]
  _GroupVersion = 1
